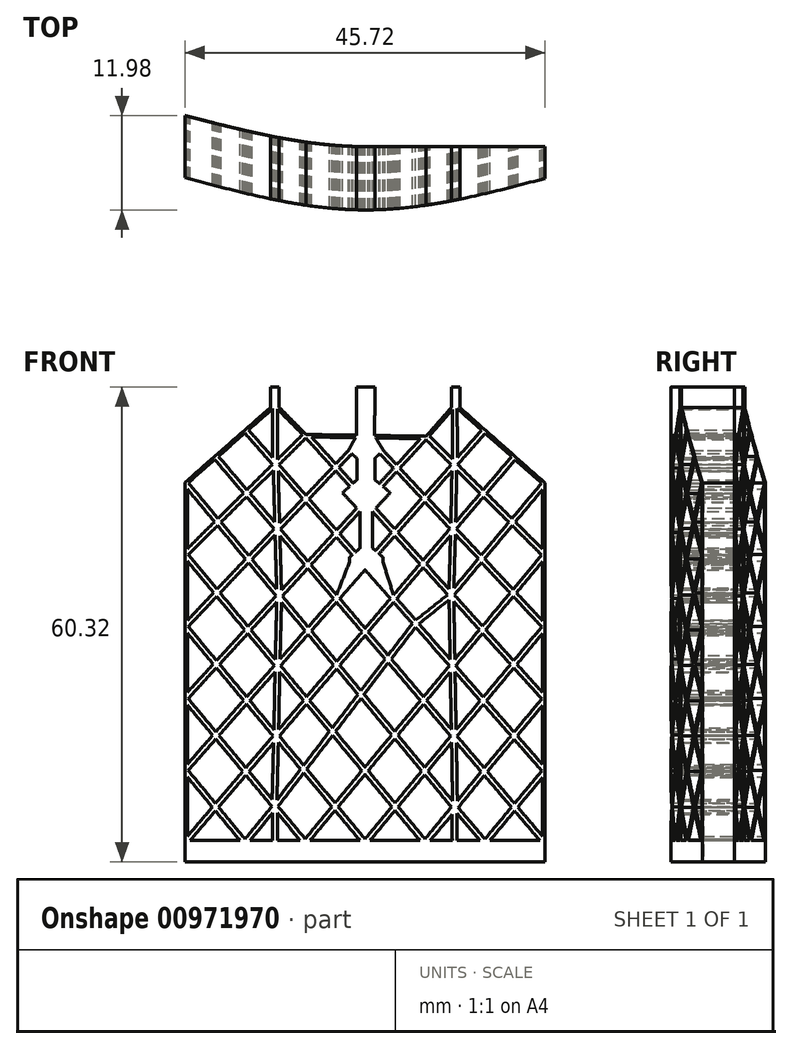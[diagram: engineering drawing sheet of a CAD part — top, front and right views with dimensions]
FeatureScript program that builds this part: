
annotation { "Feature Type Name" : "Feature", "Feature Type Description" : "" }
export const myFeature = defineFeature(function(context is Context, id is Id, definition is map)
    precondition{}
    {
        {
            var Q0;
            Q0=qCreatedBy(makeId("Top.planeOp"),FACE);
            var sketch = newSketch(context, id + "F0", { "sketchPlane" : qUnion([Q0])});
            skLineSegment(sketch, "E0", {"start": v(0, -22.65) * mm, "end": v(38.1, -22.65) * mm});
            skLineSegment(sketch, "E1", {"start": v(38.1, -22.65) * mm, "end": v(-38.1, -22.65) * mm});
            skLineSegment(sketch, "E2", {"start": v(38.1, -22.65) * mm, "end": v(38.1, -16.26) * mm});
            skLineSegment(sketch, "E3", {"start": v(38.1, -16.26) * mm, "end": v(38.1, -29.4) * mm});
            skLineSegment(sketch, "E4", {"start": v(-38.1, -22.65) * mm, "end": v(-38.1, -29.22) * mm});
            skLineSegment(sketch, "E5", {"start": v(-38.1, -29.22) * mm, "end": v(-38.1, -16.09) * mm});
            skPoint(sketch, "E6", {"position": v(-38.1, -22.65) * mm});
            skPoint(sketch, "E7", {"position": v(38.1, -22.82) * mm});
            skFitSpline(sketch, "E8", {"points": [v(-38.1, -16.09) * mm, v(0, -22.65) * mm, v(38.1, -16.26) * mm], "startDerivative": vector(76.18, -19.61) * mm, "endDerivative": vector(76.22, 19.27) * mm});
            skLineSegment(sketch, "E9", {"start": v(0, -22.65) * mm, "end": v(0, -36.06) * mm});
            skFitSpline(sketch, "E10", {"points": [v(-38.1, -29.22) * mm, v(0, -36.06) * mm, v(38.1, -29.4) * mm], "startDerivative": vector(76.18, -20.42) * mm, "endDerivative": vector(76.22, 20.08) * mm});
            skSolve(sketch);
        }
        {
            var Q0;
            Q0=qCreatedBy(makeId("Front.planeOp"),FACE);
            var sketch = newSketch(context, id + "F1", { "sketchPlane" : qUnion([Q0])});
            skLineSegment(sketch, "E11", {"start": v(38.1, -46.22) * mm, "end": v(25.4, -46.22) * mm, "construction": true});
            skLineSegment(sketch, "E12", {"start": v(-38.1, -46.22) * mm, "end": v(-38.1, -30.9) * mm, "construction": true});
            skLineSegment(sketch, "E13", {"start": v(38.1, 29.98) * mm, "end": v(38.1, 14.74) * mm, "construction": true});
            skLineSegment(sketch, "E14", {"start": v(-38.1, 30.06) * mm, "end": v(-31.74, 35.65) * mm, "construction": true});
            skLineSegment(sketch, "E15", {"start": v(38.1, 29.98) * mm, "end": v(31.76, 35.6) * mm, "construction": true});
            skLineSegment(sketch, "E16", {"start": v(-19.02, 46.83) * mm, "end": v(-12.48, 40.22) * mm, "construction": true});
            skLineSegment(sketch, "E17", {"start": v(19.08, 46.82) * mm, "end": v(12.92, 39.85) * mm, "construction": true});
            skLineSegment(sketch, "E18", {"start": v(-12.48, 40.22) * mm, "end": v(0.22, 40.04) * mm, "construction": true});
            skLineSegment(sketch, "E19", {"start": v(-25.38, 41.24) * mm, "end": v(-19.02, 46.83) * mm, "construction": true});
            skLineSegment(sketch, "E20", {"start": v(-31.74, 35.65) * mm, "end": v(-25.38, 41.24) * mm, "construction": true});
            skLineSegment(sketch, "E21", {"start": v(25.42, 41.2) * mm, "end": v(19.08, 46.82) * mm, "construction": true});
            skLineSegment(sketch, "E22", {"start": v(31.76, 35.6) * mm, "end": v(25.42, 41.2) * mm, "construction": true});
            skLineSegment(sketch, "E23", {"start": v(38.1, 14.74) * mm, "end": v(38.1, -0.5) * mm, "construction": true});
            skLineSegment(sketch, "E24", {"start": v(38.1, -0.5) * mm, "end": v(38.1, -15.74) * mm, "construction": true});
            skLineSegment(sketch, "E25", {"start": v(38.1, -15.74) * mm, "end": v(38.1, -30.98) * mm, "construction": true});
            skLineSegment(sketch, "E26", {"start": v(38.1, -30.98) * mm, "end": v(38.1, -46.22) * mm, "construction": true});
            skLineSegment(sketch, "E27", {"start": v(-38.1, 14.82) * mm, "end": v(-38.1, 30.06) * mm, "construction": true});
            skLineSegment(sketch, "E28", {"start": v(-38.1, -0.42) * mm, "end": v(-38.1, 14.82) * mm, "construction": true});
            skLineSegment(sketch, "E29", {"start": v(-38.1, -15.66) * mm, "end": v(-38.1, -0.42) * mm, "construction": true});
            skLineSegment(sketch, "E30", {"start": v(-38.1, -30.9) * mm, "end": v(-38.1, -15.66) * mm, "construction": true});
            skLineSegment(sketch, "E31", {"start": v(-25.4, -46.22) * mm, "end": v(-38.1, -46.22) * mm, "construction": true});
            skLineSegment(sketch, "E32", {"start": v(-12.64, -46.22) * mm, "end": v(-19.02, -46.22) * mm, "construction": true});
            skLineSegment(sketch, "E33", {"start": v(-50.8, 0) * mm, "end": v(-50.8, 0) * mm});
            skLineSegment(sketch, "E34", {"start": v(12.7, -46.22) * mm, "end": v(0, -46.22) * mm, "construction": true});
            skLineSegment(sketch, "E35", {"start": v(25.4, -46.22) * mm, "end": v(18.98, -46.22) * mm, "construction": true});
            skLineSegment(sketch, "E36", {"start": v(0, -46.22) * mm, "end": v(-12.7, -46.22) * mm, "construction": true});
            skLineSegment(sketch, "E37", {"start": v(12.92, 39.85) * mm, "end": v(18.94, 33.85) * mm, "construction": true});
            skPoint(sketch, "E38", {"position": v(0.22, 40.04) * mm});
            skLineSegment(sketch, "E39", {"start": v(-12.48, 40.22) * mm, "end": v(-6.2, 33.27) * mm, "construction": true});
            skLineSegment(sketch, "E40", {"start": v(0.22, 40.04) * mm, "end": v(6.7, 33.1) * mm, "construction": true});
            skLineSegment(sketch, "E41", {"start": v(-25.38, 41.24) * mm, "end": v(-18.99, 33.96) * mm, "construction": true});
            skLineSegment(sketch, "E42", {"start": v(-31.74, 35.65) * mm, "end": v(-25.03, 27.78) * mm, "construction": true});
            skLineSegment(sketch, "E43", {"start": v(-38.1, 30.06) * mm, "end": v(-31.16, 21.7) * mm, "construction": true});
            skLineSegment(sketch, "E44", {"start": v(-38.1, -0.42) * mm, "end": v(-31.45, -8.42) * mm, "construction": true});
            skLineSegment(sketch, "E45", {"start": v(-38.1, -15.66) * mm, "end": v(-31.58, -23.49) * mm, "construction": true});
            skLineSegment(sketch, "E46", {"start": v(-38.1, -30.9) * mm, "end": v(-31.66, -38.67) * mm, "construction": true});
            skLineSegment(sketch, "E47", {"start": v(-12.48, 40.22) * mm, "end": v(-18.9, 33.86) * mm, "construction": true});
            skLineSegment(sketch, "E48", {"start": v(0.22, 40.04) * mm, "end": v(-6.2, 33.27) * mm, "construction": true});
            skLineSegment(sketch, "E49", {"start": v(12.92, 39.85) * mm, "end": v(6.7, 33.1) * mm, "construction": true});
            skLineSegment(sketch, "E50", {"start": v(25.42, 41.2) * mm, "end": v(19.08, 34) * mm, "construction": true});
            skLineSegment(sketch, "E51", {"start": v(31.76, 35.6) * mm, "end": v(25.06, 27.75) * mm, "construction": true});
            skLineSegment(sketch, "E52", {"start": v(38.1, 29.98) * mm, "end": v(31.15, 21.68) * mm, "construction": true});
            skLineSegment(sketch, "E53", {"start": v(38.1, 14.74) * mm, "end": v(31.38, 6.68) * mm, "construction": true});
            skLineSegment(sketch, "E54", {"start": v(38.1, -0.5) * mm, "end": v(31.49, -8.43) * mm, "construction": true});
            skLineSegment(sketch, "E55", {"start": v(38.1, -30.98) * mm, "end": v(31.68, -38.69) * mm, "construction": true});
            skLineSegment(sketch, "E56", {"start": v(-38.1, 14.82) * mm, "end": v(-31.35, 6.7) * mm, "construction": true});
            skLineSegment(sketch, "E57", {"start": v(38.1, -15.74) * mm, "end": v(31.58, -23.56) * mm, "construction": true});
            skLineSegment(sketch, "E58", {"start": v(0.22, 40.04) * mm, "end": v(12.92, 39.85) * mm, "construction": true});
            skLineSegment(sketch, "E59", {"start": v(19.08, 34) * mm, "end": v(18.94, 33.85) * mm, "construction": true});
            skLineSegment(sketch, "E60", {"start": v(18.94, 33.85) * mm, "end": v(19.08, 33.71) * mm, "construction": true});
            skLineSegment(sketch, "E61", {"start": v(19.08, 33.71) * mm, "end": v(25.06, 27.75) * mm, "construction": true});
            skLineSegment(sketch, "E62", {"start": v(18.67, 20.27) * mm, "end": v(12.3, 12.81) * mm, "construction": true});
            skLineSegment(sketch, "E63", {"start": v(18.54, -8.73) * mm, "end": v(12.4, -16.1) * mm, "construction": true});
            skLineSegment(sketch, "E64", {"start": v(18.83, -23.63) * mm, "end": v(12.64, -31.04) * mm, "construction": true});
            skLineSegment(sketch, "E65", {"start": v(18.98, -46.22) * mm, "end": v(12.7, -46.22) * mm, "construction": true});
            skLineSegment(sketch, "E66", {"start": v(18.94, 33.85) * mm, "end": v(12.66, 26.71) * mm, "construction": true});
            skLineSegment(sketch, "E67", {"start": v(25.06, 27.75) * mm, "end": v(18.67, 20.27) * mm, "construction": true});
            skLineSegment(sketch, "E68", {"start": v(25.06, 27.75) * mm, "end": v(31.15, 21.68) * mm, "construction": true});
            skLineSegment(sketch, "E69", {"start": v(31.15, 21.68) * mm, "end": v(24.67, 13.94) * mm, "construction": true});
            skLineSegment(sketch, "E70", {"start": v(31.15, 21.68) * mm, "end": v(38.1, 14.74) * mm, "construction": true});
            skLineSegment(sketch, "E71.0", {"start": v(24.7, 41.16) * mm, "end": v(19.5, 45.76) * mm});
            skLineSegment(sketch, "E71.1", {"start": v(24.7, 41.16) * mm, "end": v(19.59, 35.35) * mm});
            skLineSegment(sketch, "E71.2", {"start": v(19.5, 45.76) * mm, "end": v(19.59, 35.35) * mm});
            skLineSegment(sketch, "E72.0", {"start": v(18.56, 45.52) * mm, "end": v(18.56, 35.03) * mm});
            skLineSegment(sketch, "E72.1", {"start": v(18.56, 45.52) * mm, "end": v(13.63, 39.95) * mm});
            skLineSegment(sketch, "E72.2", {"start": v(13.63, 39.95) * mm, "end": v(18.56, 35.03) * mm});
            skLineSegment(sketch, "E73.0", {"start": v(31.05, 35.54) * mm, "end": v(25.46, 40.49) * mm});
            skLineSegment(sketch, "E73.1", {"start": v(31.05, 35.54) * mm, "end": v(25.03, 28.5) * mm});
            skLineSegment(sketch, "E73.2", {"start": v(19.64, 33.87) * mm, "end": v(25.03, 28.5) * mm});
            skLineSegment(sketch, "E73.3", {"start": v(25.46, 40.49) * mm, "end": v(19.64, 33.87) * mm});
            skLineSegment(sketch, "E74.0", {"start": v(37.4, 29.93) * mm, "end": v(31.8, 34.87) * mm});
            skLineSegment(sketch, "E74.1", {"start": v(37.4, 29.93) * mm, "end": v(31.11, 22.43) * mm});
            skLineSegment(sketch, "E74.2", {"start": v(25.75, 27.77) * mm, "end": v(31.11, 22.43) * mm});
            skLineSegment(sketch, "E74.3", {"start": v(31.8, 34.87) * mm, "end": v(25.75, 27.77) * mm});
            skLineSegment(sketch, "E75.0", {"start": v(37.6, 28.58) * mm, "end": v(37.6, 15.97) * mm});
            skLineSegment(sketch, "E75.1", {"start": v(37.6, 28.58) * mm, "end": v(31.83, 21.7) * mm});
            skLineSegment(sketch, "E75.2", {"start": v(31.83, 21.7) * mm, "end": v(37.6, 15.97) * mm});
            skLineSegment(sketch, "E76", {"start": v(-18.99, 33.96) * mm, "end": v(-18.9, 33.86) * mm, "construction": true});
            skLineSegment(sketch, "E77", {"start": v(-18.9, 33.86) * mm, "end": v(-19.02, 33.73) * mm, "construction": true});
            skLineSegment(sketch, "E78", {"start": v(-18.9, 33.86) * mm, "end": v(-12.51, 26.6) * mm, "construction": true});
            skLineSegment(sketch, "E79", {"start": v(-19.02, 33.73) * mm, "end": v(-25.03, 27.78) * mm, "construction": true});
            skLineSegment(sketch, "E80", {"start": v(-18.57, 20.2) * mm, "end": v(-12.1, 12.63) * mm, "construction": true});
            skLineSegment(sketch, "E81", {"start": v(-18.57, 20.2) * mm, "end": v(-24.61, 13.82) * mm, "construction": true});
            skLineSegment(sketch, "E82", {"start": v(-18.15, 6.04) * mm, "end": v(-12.03, -1.33) * mm, "construction": true});
            skLineSegment(sketch, "E83", {"start": v(-18.15, 6.04) * mm, "end": v(-24.8, -1.19) * mm, "construction": true});
            skLineSegment(sketch, "E84", {"start": v(-18.8, -23.62) * mm, "end": v(-12.98, -30.62) * mm, "construction": true});
            skLineSegment(sketch, "E85", {"start": v(-18.8, -23.62) * mm, "end": v(-25.23, -31.14) * mm, "construction": true});
            skLineSegment(sketch, "E86", {"start": v(-19.19, -38.36) * mm, "end": v(-12.64, -46.22) * mm, "construction": true});
            skLineSegment(sketch, "E87", {"start": v(-19.05, -38.52) * mm, "end": v(-25.4, -46.22) * mm, "construction": true});
            skLineSegment(sketch, "E88", {"start": v(-19.02, -46.22) * mm, "end": v(-25.4, -46.22) * mm, "construction": true});
            skLineSegment(sketch, "E89", {"start": v(-25.03, 27.78) * mm, "end": v(-18.57, 20.2) * mm, "construction": true});
            skLineSegment(sketch, "E90", {"start": v(-25.03, 27.78) * mm, "end": v(-31.16, 21.7) * mm, "construction": true});
            skLineSegment(sketch, "E91", {"start": v(-31.16, 21.7) * mm, "end": v(-24.61, 13.82) * mm, "construction": true});
            skLineSegment(sketch, "E92", {"start": v(-31.16, 21.7) * mm, "end": v(-38.1, 14.82) * mm, "construction": true});
            skLineSegment(sketch, "E93.0", {"start": v(-37.4, 30) * mm, "end": v(-31.8, 34.93) * mm});
            skLineSegment(sketch, "E93.1", {"start": v(-37.4, 30) * mm, "end": v(-31.12, 22.45) * mm});
            skLineSegment(sketch, "E93.2", {"start": v(-25.72, 27.8) * mm, "end": v(-31.12, 22.45) * mm});
            skLineSegment(sketch, "E93.3", {"start": v(-31.8, 34.93) * mm, "end": v(-25.72, 27.8) * mm});
            skLineSegment(sketch, "E94.0", {"start": v(-37.6, 28.65) * mm, "end": v(-31.85, 21.73) * mm});
            skLineSegment(sketch, "E94.1", {"start": v(-37.6, 16.04) * mm, "end": v(-37.6, 28.65) * mm});
            skLineSegment(sketch, "E94.2", {"start": v(-31.85, 21.73) * mm, "end": v(-37.6, 16.04) * mm});
            skLineSegment(sketch, "E95", {"start": v(-6.2, 33.27) * mm, "end": v(0.28, 26.1) * mm, "construction": true});
            skLineSegment(sketch, "E96", {"start": v(-6.2, 33.27) * mm, "end": v(-12.51, 26.6) * mm, "construction": true});
            skLineSegment(sketch, "E97", {"start": v(6.7, 33.1) * mm, "end": v(12.66, 26.71) * mm, "construction": true});
            skLineSegment(sketch, "E98", {"start": v(6.7, 33.1) * mm, "end": v(0.28, 26.1) * mm, "construction": true});
            skLineSegment(sketch, "E99.0", {"start": v(-11.32, 39.7) * mm, "end": v(-6.18, 34.02) * mm});
            skLineSegment(sketch, "E99.1", {"start": v(-11.32, 39.7) * mm, "end": v(-0.95, 39.55) * mm});
            skLineSegment(sketch, "E99.2", {"start": v(-0.95, 39.55) * mm, "end": v(-6.18, 34.02) * mm});
            skLineSegment(sketch, "E100.0", {"start": v(1.4, 39.51) * mm, "end": v(11.78, 39.36) * mm});
            skLineSegment(sketch, "E100.1", {"start": v(1.4, 39.51) * mm, "end": v(6.7, 33.84) * mm});
            skLineSegment(sketch, "E100.2", {"start": v(11.78, 39.36) * mm, "end": v(6.7, 33.84) * mm});
            skLineSegment(sketch, "E101", {"start": v(0.28, 26.1) * mm, "end": v(-6.04, 19.23) * mm, "construction": true});
            skLineSegment(sketch, "E102", {"start": v(0.28, 26.1) * mm, "end": v(6.28, 19.47) * mm, "construction": true});
            skLineSegment(sketch, "E103", {"start": v(-12.51, 26.6) * mm, "end": v(-18.57, 20.2) * mm, "construction": true});
            skLineSegment(sketch, "E104", {"start": v(-6.04, 19.23) * mm, "end": v(-12.1, 12.63) * mm, "construction": true});
            skLineSegment(sketch, "E105", {"start": v(-6.04, 19.23) * mm, "end": v(0.01, 12.35) * mm, "construction": true});
            skLineSegment(sketch, "E106", {"start": v(-12.51, 26.6) * mm, "end": v(-6.04, 19.23) * mm, "construction": true});
            skLineSegment(sketch, "E107", {"start": v(12.66, 26.71) * mm, "end": v(18.67, 20.27) * mm, "construction": true});
            skLineSegment(sketch, "E108", {"start": v(12.66, 26.71) * mm, "end": v(6.28, 19.47) * mm, "construction": true});
            skLineSegment(sketch, "E109", {"start": v(6.28, 19.47) * mm, "end": v(0.01, 12.35) * mm, "construction": true});
            skLineSegment(sketch, "E110", {"start": v(6.28, 19.47) * mm, "end": v(12.3, 12.81) * mm, "construction": true});
            skLineSegment(sketch, "E111.0", {"start": v(12.93, 39.12) * mm, "end": v(18.24, 33.82) * mm});
            skLineSegment(sketch, "E111.1", {"start": v(12.93, 39.12) * mm, "end": v(7.4, 33.1) * mm});
            skLineSegment(sketch, "E111.2", {"start": v(7.4, 33.1) * mm, "end": v(12.65, 27.47) * mm});
            skLineSegment(sketch, "E111.3", {"start": v(18.24, 33.82) * mm, "end": v(12.65, 27.47) * mm});
            skLineSegment(sketch, "E112.0", {"start": v(6.7, 32.34) * mm, "end": v(11.97, 26.7) * mm});
            skLineSegment(sketch, "E112.1", {"start": v(6.7, 32.34) * mm, "end": v(0.97, 26.1) * mm});
            skLineSegment(sketch, "E112.2", {"start": v(0.97, 26.1) * mm, "end": v(6.28, 20.24) * mm});
            skLineSegment(sketch, "E112.3", {"start": v(11.97, 26.7) * mm, "end": v(6.28, 20.24) * mm});
            skLineSegment(sketch, "E113.0", {"start": v(0.22, 39.3) * mm, "end": v(6, 33.09) * mm});
            skLineSegment(sketch, "E113.1", {"start": v(0.22, 39.3) * mm, "end": v(-5.5, 33.26) * mm});
            skLineSegment(sketch, "E113.2", {"start": v(-5.5, 33.26) * mm, "end": v(0.29, 26.86) * mm});
            skLineSegment(sketch, "E113.3", {"start": v(6, 33.09) * mm, "end": v(0.29, 26.86) * mm});
            skLineSegment(sketch, "E114.0", {"start": v(-6.2, 32.52) * mm, "end": v(-0.4, 26.1) * mm});
            skLineSegment(sketch, "E114.1", {"start": v(-6.2, 32.52) * mm, "end": v(-11.82, 26.58) * mm});
            skLineSegment(sketch, "E114.2", {"start": v(-11.82, 26.58) * mm, "end": v(-6.03, 19.99) * mm});
            skLineSegment(sketch, "E114.3", {"start": v(-0.4, 26.1) * mm, "end": v(-6.03, 19.99) * mm});
            skLineSegment(sketch, "E115.0", {"start": v(-6.88, 33.28) * mm, "end": v(-12.5, 27.35) * mm});
            skLineSegment(sketch, "E115.1", {"start": v(-12.5, 39.49) * mm, "end": v(-6.88, 33.28) * mm});
            skLineSegment(sketch, "E115.2", {"start": v(-12.5, 39.49) * mm, "end": v(-18.2, 33.84) * mm});
            skLineSegment(sketch, "E115.3", {"start": v(-18.2, 33.84) * mm, "end": v(-12.5, 27.35) * mm});
            skLineSegment(sketch, "E116.0", {"start": v(-18.51, 45.6) * mm, "end": v(-13.2, 40.22) * mm});
            skLineSegment(sketch, "E116.1", {"start": v(-18.51, 45.6) * mm, "end": v(-18.51, 34.95) * mm});
            skLineSegment(sketch, "E116.2", {"start": v(-13.2, 40.22) * mm, "end": v(-18.51, 34.95) * mm});
            skLineSegment(sketch, "E117.0", {"start": v(-19.53, 45.7) * mm, "end": v(-19.53, 35.36) * mm});
            skLineSegment(sketch, "E117.1", {"start": v(-24.66, 41.2) * mm, "end": v(-19.53, 45.7) * mm});
            skLineSegment(sketch, "E117.2", {"start": v(-24.66, 41.2) * mm, "end": v(-19.53, 35.36) * mm});
            skLineSegment(sketch, "E118.0", {"start": v(-25.43, 40.52) * mm, "end": v(-19.6, 33.88) * mm});
            skLineSegment(sketch, "E118.1", {"start": v(-31.03, 35.6) * mm, "end": v(-25.43, 40.52) * mm});
            skLineSegment(sketch, "E118.2", {"start": v(-31.03, 35.6) * mm, "end": v(-25, 28.53) * mm});
            skLineSegment(sketch, "E118.3", {"start": v(-19.6, 33.88) * mm, "end": v(-25, 28.53) * mm});
            skLineSegment(sketch, "E119", {"start": v(31.38, 6.68) * mm, "end": v(24.89, -1.11) * mm, "construction": true});
            skLineSegment(sketch, "E120", {"start": v(31.38, 6.68) * mm, "end": v(38.1, -0.5) * mm, "construction": true});
            skLineSegment(sketch, "E121", {"start": v(31.49, -8.43) * mm, "end": v(25.06, -16.14) * mm, "construction": true});
            skLineSegment(sketch, "E122", {"start": v(31.49, -8.43) * mm, "end": v(38.1, -15.74) * mm, "construction": true});
            skLineSegment(sketch, "E123", {"start": v(31.58, -23.56) * mm, "end": v(25.25, -31.16) * mm, "construction": true});
            skLineSegment(sketch, "E124", {"start": v(31.58, -23.56) * mm, "end": v(38.1, -30.98) * mm, "construction": true});
            skLineSegment(sketch, "E125", {"start": v(31.68, -38.69) * mm, "end": v(25.4, -46.22) * mm, "construction": true});
            skLineSegment(sketch, "E126", {"start": v(31.68, -38.69) * mm, "end": v(38.1, -46.22) * mm, "construction": true});
            skLineSegment(sketch, "E127.0", {"start": v(37.6, 13.35) * mm, "end": v(32.05, 6.7) * mm});
            skLineSegment(sketch, "E127.1", {"start": v(37.6, 13.35) * mm, "end": v(37.6, 0.78) * mm});
            skLineSegment(sketch, "E127.2", {"start": v(32.05, 6.7) * mm, "end": v(37.6, 0.78) * mm});
            skLineSegment(sketch, "E128.0", {"start": v(37.6, -1.9) * mm, "end": v(32.16, -8.42) * mm});
            skLineSegment(sketch, "E128.1", {"start": v(37.6, -1.9) * mm, "end": v(37.6, -14.42) * mm});
            skLineSegment(sketch, "E128.2", {"start": v(32.16, -8.42) * mm, "end": v(37.6, -14.42) * mm});
            skLineSegment(sketch, "E129.0", {"start": v(37.6, -17.14) * mm, "end": v(32.25, -23.55) * mm});
            skLineSegment(sketch, "E129.1", {"start": v(37.6, -17.14) * mm, "end": v(37.6, -29.63) * mm});
            skLineSegment(sketch, "E129.2", {"start": v(32.25, -23.55) * mm, "end": v(37.6, -29.63) * mm});
            skLineSegment(sketch, "E130.0", {"start": v(37.6, -32.38) * mm, "end": v(32.34, -38.68) * mm});
            skLineSegment(sketch, "E130.1", {"start": v(37.6, -32.38) * mm, "end": v(37.6, -44.84) * mm});
            skLineSegment(sketch, "E130.2", {"start": v(32.34, -38.68) * mm, "end": v(37.6, -44.84) * mm});
            skLineSegment(sketch, "E131", {"start": v(-31.35, 6.7) * mm, "end": v(-24.79, -1.18) * mm, "construction": true});
            skLineSegment(sketch, "E132", {"start": v(-31.35, 6.7) * mm, "end": v(-38.1, -0.42) * mm, "construction": true});
            skLineSegment(sketch, "E133", {"start": v(-31.45, -8.42) * mm, "end": v(-25.05, -16.11) * mm, "construction": true});
            skLineSegment(sketch, "E134", {"start": v(-31.45, -8.42) * mm, "end": v(-38.1, -15.66) * mm, "construction": true});
            skLineSegment(sketch, "E135", {"start": v(-31.58, -23.49) * mm, "end": v(-25.21, -31.13) * mm, "construction": true});
            skLineSegment(sketch, "E136", {"start": v(-31.58, -23.49) * mm, "end": v(-38.1, -30.9) * mm, "construction": true});
            skLineSegment(sketch, "E137", {"start": v(-31.66, -38.67) * mm, "end": v(-38.1, -46.22) * mm, "construction": true});
            skLineSegment(sketch, "E138", {"start": v(-31.66, -38.67) * mm, "end": v(-25.4, -46.22) * mm, "construction": true});
            skLineSegment(sketch, "E139.0", {"start": v(-37.6, 13.41) * mm, "end": v(-32.03, 6.73) * mm});
            skLineSegment(sketch, "E139.1", {"start": v(-37.6, 0.85) * mm, "end": v(-37.6, 13.41) * mm});
            skLineSegment(sketch, "E139.2", {"start": v(-32.03, 6.73) * mm, "end": v(-37.6, 0.85) * mm});
            skLineSegment(sketch, "E140.0", {"start": v(-37.6, -1.83) * mm, "end": v(-32.12, -8.4) * mm});
            skLineSegment(sketch, "E140.1", {"start": v(-37.6, -14.36) * mm, "end": v(-37.6, -1.83) * mm});
            skLineSegment(sketch, "E140.2", {"start": v(-32.12, -8.4) * mm, "end": v(-37.6, -14.36) * mm});
            skLineSegment(sketch, "E141.0", {"start": v(-37.6, -17.04) * mm, "end": v(-32.24, -23.48) * mm});
            skLineSegment(sketch, "E141.1", {"start": v(-37.6, -29.58) * mm, "end": v(-37.6, -17.04) * mm});
            skLineSegment(sketch, "E141.2", {"start": v(-32.24, -23.48) * mm, "end": v(-37.6, -29.58) * mm});
            skLineSegment(sketch, "E142.0", {"start": v(-37.6, -44.85) * mm, "end": v(-37.6, -32.3) * mm});
            skLineSegment(sketch, "E142.1", {"start": v(-32.31, -38.67) * mm, "end": v(-37.6, -44.85) * mm});
            skLineSegment(sketch, "E142.2", {"start": v(-37.6, -32.3) * mm, "end": v(-32.31, -38.67) * mm});
            skLineSegment(sketch, "E143.0", {"start": v(-31.66, -39.46) * mm, "end": v(-37, -45.7) * mm});
            skLineSegment(sketch, "E143.1", {"start": v(-31.66, -39.46) * mm, "end": v(-26.48, -45.7) * mm});
            skLineSegment(sketch, "E143.2", {"start": v(-26.48, -45.7) * mm, "end": v(-37, -45.7) * mm});
            skLineSegment(sketch, "E144", {"start": v(-6.34, -38.6) * mm, "end": v(0, -46.22) * mm, "construction": true});
            skLineSegment(sketch, "E145", {"start": v(-6.34, -38.6) * mm, "end": v(-12.7, -46.22) * mm, "construction": true});
            skLineSegment(sketch, "E146.0", {"start": v(-6.35, -39.38) * mm, "end": v(-11.62, -45.7) * mm});
            skLineSegment(sketch, "E146.1", {"start": v(-6.35, -39.38) * mm, "end": v(-1.08, -45.7) * mm});
            skLineSegment(sketch, "E146.2", {"start": v(-1.08, -45.7) * mm, "end": v(-11.62, -45.7) * mm});
            skLineSegment(sketch, "E147.0", {"start": v(37, -45.7) * mm, "end": v(26.48, -45.7) * mm});
            skLineSegment(sketch, "E147.1", {"start": v(31.68, -39.47) * mm, "end": v(37, -45.7) * mm});
            skLineSegment(sketch, "E147.2", {"start": v(31.68, -39.47) * mm, "end": v(26.48, -45.7) * mm});
            skLineSegment(sketch, "E148", {"start": v(-24.61, 13.82) * mm, "end": v(-18.15, 6.04) * mm, "construction": true});
            skLineSegment(sketch, "E149", {"start": v(-24.61, 13.82) * mm, "end": v(-31.35, 6.7) * mm, "construction": true});
            skLineSegment(sketch, "E150", {"start": v(-24.8, -1.19) * mm, "end": v(-31.45, -8.42) * mm, "construction": true});
            skLineSegment(sketch, "E151", {"start": v(-25.05, -16.11) * mm, "end": v(-18.8, -23.62) * mm, "construction": true});
            skLineSegment(sketch, "E152", {"start": v(-25.07, -16.09) * mm, "end": v(-31.58, -23.49) * mm, "construction": true});
            skLineSegment(sketch, "E153", {"start": v(-25.23, -31.14) * mm, "end": v(-31.66, -38.67) * mm, "construction": true});
            skLineSegment(sketch, "E154", {"start": v(-25.21, -31.13) * mm, "end": v(-19.19, -38.36) * mm, "construction": true});
            skLineSegment(sketch, "E155.0", {"start": v(-31.2, 20.95) * mm, "end": v(-25.3, 13.84) * mm});
            skLineSegment(sketch, "E155.1", {"start": v(-31.2, 20.95) * mm, "end": v(-37.41, 14.79) * mm});
            skLineSegment(sketch, "E155.2", {"start": v(-37.41, 14.79) * mm, "end": v(-31.32, 7.47) * mm});
            skLineSegment(sketch, "E155.3", {"start": v(-25.3, 13.84) * mm, "end": v(-31.32, 7.47) * mm});
            skLineSegment(sketch, "E156", {"start": v(-24.79, -1.18) * mm, "end": v(-18.53, -8.7) * mm, "construction": true});
            skLineSegment(sketch, "E157.0", {"start": v(-31.37, 5.94) * mm, "end": v(-25.46, -1.16) * mm});
            skLineSegment(sketch, "E157.1", {"start": v(-31.37, 5.94) * mm, "end": v(-37.42, -0.44) * mm});
            skLineSegment(sketch, "E157.2", {"start": v(-37.42, -0.44) * mm, "end": v(-31.43, -7.65) * mm});
            skLineSegment(sketch, "E157.3", {"start": v(-25.46, -1.16) * mm, "end": v(-31.43, -7.65) * mm});
            skLineSegment(sketch, "E158.0", {"start": v(-31.46, -9.18) * mm, "end": v(-25.72, -16.08) * mm});
            skLineSegment(sketch, "E158.1", {"start": v(-31.46, -9.18) * mm, "end": v(-37.44, -15.68) * mm});
            skLineSegment(sketch, "E158.2", {"start": v(-37.44, -15.68) * mm, "end": v(-31.57, -22.72) * mm});
            skLineSegment(sketch, "E158.3", {"start": v(-25.72, -16.08) * mm, "end": v(-31.57, -22.72) * mm});
            skLineSegment(sketch, "E159.0", {"start": v(-31.59, -24.27) * mm, "end": v(-25.88, -31.12) * mm});
            skLineSegment(sketch, "E159.1", {"start": v(-31.59, -24.27) * mm, "end": v(-37.43, -30.91) * mm});
            skLineSegment(sketch, "E159.2", {"start": v(-37.43, -30.91) * mm, "end": v(-31.65, -37.88) * mm});
            skLineSegment(sketch, "E159.3", {"start": v(-25.88, -31.12) * mm, "end": v(-31.65, -37.88) * mm});
            skLineSegment(sketch, "E160", {"start": v(24.63, 13.9) * mm, "end": v(31.38, 6.68) * mm, "construction": true});
            skLineSegment(sketch, "E161", {"start": v(24.89, -1.11) * mm, "end": v(18.54, -8.73) * mm, "construction": true});
            skLineSegment(sketch, "E162", {"start": v(24.88, -1.13) * mm, "end": v(31.49, -8.43) * mm, "construction": true});
            skLineSegment(sketch, "E163", {"start": v(25.06, -16.14) * mm, "end": v(18.83, -23.63) * mm, "construction": true});
            skLineSegment(sketch, "E164", {"start": v(25.06, -16.14) * mm, "end": v(31.58, -23.56) * mm, "construction": true});
            skLineSegment(sketch, "E165", {"start": v(25.25, -31.16) * mm, "end": v(31.68, -38.69) * mm, "construction": true});
            skLineSegment(sketch, "E166.0", {"start": v(31.18, 20.93) * mm, "end": v(25.3, 13.91) * mm});
            skLineSegment(sketch, "E166.1", {"start": v(31.18, 20.93) * mm, "end": v(37.41, 14.71) * mm});
            skLineSegment(sketch, "E166.2", {"start": v(37.41, 14.71) * mm, "end": v(31.36, 7.45) * mm});
            skLineSegment(sketch, "E166.3", {"start": v(25.3, 13.91) * mm, "end": v(31.36, 7.45) * mm});
            skLineSegment(sketch, "E167.0", {"start": v(31.4, 5.92) * mm, "end": v(25.55, -1.11) * mm});
            skLineSegment(sketch, "E167.1", {"start": v(31.4, 5.92) * mm, "end": v(37.42, -0.52) * mm});
            skLineSegment(sketch, "E167.2", {"start": v(37.42, -0.52) * mm, "end": v(31.47, -7.66) * mm});
            skLineSegment(sketch, "E167.3", {"start": v(25.55, -1.11) * mm, "end": v(31.47, -7.66) * mm});
            skLineSegment(sketch, "E168.0", {"start": v(31.5, -9.2) * mm, "end": v(25.73, -16.14) * mm});
            skLineSegment(sketch, "E168.1", {"start": v(31.5, -9.2) * mm, "end": v(37.43, -15.75) * mm});
            skLineSegment(sketch, "E168.2", {"start": v(37.43, -15.75) * mm, "end": v(31.57, -22.78) * mm});
            skLineSegment(sketch, "E168.3", {"start": v(25.73, -16.14) * mm, "end": v(31.57, -22.78) * mm});
            skLineSegment(sketch, "E169.0", {"start": v(31.6, -24.34) * mm, "end": v(25.92, -31.15) * mm});
            skLineSegment(sketch, "E169.1", {"start": v(31.6, -24.34) * mm, "end": v(37.43, -30.99) * mm});
            skLineSegment(sketch, "E169.2", {"start": v(37.43, -30.99) * mm, "end": v(31.67, -37.9) * mm});
            skLineSegment(sketch, "E169.3", {"start": v(25.92, -31.15) * mm, "end": v(31.67, -37.9) * mm});
            skLineSegment(sketch, "E170", {"start": v(0.01, 12.35) * mm, "end": v(6.05, 5.48) * mm, "construction": true});
            skLineSegment(sketch, "E171", {"start": v(0.01, 12.35) * mm, "end": v(-6.02, 5.5) * mm, "construction": true});
            skLineSegment(sketch, "E172.0", {"start": v(-5.35, 19.22) * mm, "end": v(0.01, 13.12) * mm});
            skLineSegment(sketch, "E172.1", {"start": v(0.28, 25.35) * mm, "end": v(-5.35, 19.22) * mm});
            skLineSegment(sketch, "E172.2", {"start": v(0.28, 25.35) * mm, "end": v(5.6, 19.47) * mm});
            skLineSegment(sketch, "E172.3", {"start": v(5.6, 19.47) * mm, "end": v(0.01, 13.12) * mm});
            skLineSegment(sketch, "E173", {"start": v(-12.1, 12.63) * mm, "end": v(-18.15, 6.04) * mm, "construction": true});
            skLineSegment(sketch, "E174", {"start": v(-6.02, 5.5) * mm, "end": v(-12.03, -1.33) * mm, "construction": true});
            skLineSegment(sketch, "E175", {"start": v(-12.1, 12.63) * mm, "end": v(-6.02, 5.5) * mm, "construction": true});
            skLineSegment(sketch, "E176", {"start": v(-6.02, 5.5) * mm, "end": v(0.02, -1.58) * mm, "construction": true});
            skLineSegment(sketch, "E177", {"start": v(12.3, 12.81) * mm, "end": v(18.3, 6.2) * mm, "construction": true});
            skLineSegment(sketch, "E178", {"start": v(6.05, 5.48) * mm, "end": v(0.02, -1.58) * mm, "construction": true});
            skLineSegment(sketch, "E179", {"start": v(6.05, 5.48) * mm, "end": v(11.99, -1.27) * mm, "construction": true});
            skLineSegment(sketch, "E180", {"start": v(12.3, 12.81) * mm, "end": v(6.05, 5.48) * mm, "construction": true});
            skLineSegment(sketch, "E181.0", {"start": v(-6.04, 18.47) * mm, "end": v(-11.42, 12.62) * mm});
            skLineSegment(sketch, "E181.1", {"start": v(-6.04, 18.47) * mm, "end": v(-0.66, 12.35) * mm});
            skLineSegment(sketch, "E181.2", {"start": v(-0.66, 12.35) * mm, "end": v(-6.01, 6.28) * mm});
            skLineSegment(sketch, "E181.3", {"start": v(-11.42, 12.62) * mm, "end": v(-6.01, 6.28) * mm});
            skLineSegment(sketch, "E182.0", {"start": v(6.29, 18.71) * mm, "end": v(0.69, 12.35) * mm});
            skLineSegment(sketch, "E182.1", {"start": v(6.29, 18.71) * mm, "end": v(11.63, 12.8) * mm});
            skLineSegment(sketch, "E182.2", {"start": v(11.63, 12.8) * mm, "end": v(6.04, 6.26) * mm});
            skLineSegment(sketch, "E182.3", {"start": v(0.69, 12.35) * mm, "end": v(6.04, 6.26) * mm});
            skLineSegment(sketch, "E183", {"start": v(0.02, -1.58) * mm, "end": v(-5.99, -8.6) * mm, "construction": true});
            skLineSegment(sketch, "E184", {"start": v(0.02, -1.58) * mm, "end": v(5.98, -8.57) * mm, "construction": true});
            skLineSegment(sketch, "E185.0", {"start": v(0.01, 11.58) * mm, "end": v(-5.35, 5.5) * mm});
            skLineSegment(sketch, "E185.1", {"start": v(0.01, 11.58) * mm, "end": v(5.38, 5.48) * mm});
            skLineSegment(sketch, "E185.2", {"start": v(5.38, 5.48) * mm, "end": v(0.02, -0.8) * mm});
            skLineSegment(sketch, "E185.3", {"start": v(-5.35, 5.5) * mm, "end": v(0.02, -0.8) * mm});
            skLineSegment(sketch, "E186", {"start": v(5.98, -8.57) * mm, "end": v(12.4, -16.1) * mm, "construction": true});
            skLineSegment(sketch, "E187", {"start": v(11.99, -1.27) * mm, "end": v(18.52, -8.7) * mm, "construction": true});
            skLineSegment(sketch, "E188", {"start": v(10.68, 0.2) * mm, "end": v(4.9, -7.31) * mm, "construction": true});
            skLineSegment(sketch, "E189", {"start": v(4.9, -7.31) * mm, "end": v(-0.84, -14.8) * mm, "construction": true});
            skLineSegment(sketch, "E190.0", {"start": v(6.05, 4.7) * mm, "end": v(0.69, -1.58) * mm});
            skLineSegment(sketch, "E190.1", {"start": v(6.05, 4.7) * mm, "end": v(10.03, 0.19) * mm});
            skLineSegment(sketch, "E190.2", {"start": v(10.03, 0.19) * mm, "end": v(4.89, -6.5) * mm});
            skLineSegment(sketch, "E190.3", {"start": v(0.69, -1.58) * mm, "end": v(4.89, -6.5) * mm});
            skLineSegment(sketch, "E191", {"start": v(-12.03, -1.33) * mm, "end": v(-18.53, -8.7) * mm, "construction": true});
            skLineSegment(sketch, "E192", {"start": v(-12.03, -1.33) * mm, "end": v(-5.99, -8.6) * mm, "construction": true});
            skLineSegment(sketch, "E193", {"start": v(-5.99, -8.6) * mm, "end": v(-0.84, -14.8) * mm, "construction": true});
            skLineSegment(sketch, "E194", {"start": v(-5.99, -8.6) * mm, "end": v(-12.4, -16.11) * mm, "construction": true});
            skLineSegment(sketch, "E195.0", {"start": v(-6.03, 4.72) * mm, "end": v(-11.37, -1.34) * mm});
            skLineSegment(sketch, "E195.1", {"start": v(-6.03, 4.72) * mm, "end": v(-0.65, -1.58) * mm});
            skLineSegment(sketch, "E195.2", {"start": v(-0.65, -1.58) * mm, "end": v(-5.98, -7.82) * mm});
            skLineSegment(sketch, "E195.3", {"start": v(-11.37, -1.34) * mm, "end": v(-5.98, -7.82) * mm});
            skLineSegment(sketch, "E196", {"start": v(-0.84, -14.8) * mm, "end": v(6.3, -23.41) * mm, "construction": true});
            skLineSegment(sketch, "E197", {"start": v(-0.84, -14.8) * mm, "end": v(-6.89, -22.68) * mm, "construction": true});
            skLineSegment(sketch, "E198", {"start": v(12.4, -16.1) * mm, "end": v(18.83, -23.63) * mm, "construction": true});
            skLineSegment(sketch, "E199", {"start": v(6.3, -23.41) * mm, "end": v(-0.02, -31) * mm, "construction": true});
            skLineSegment(sketch, "E200", {"start": v(6.3, -23.41) * mm, "end": v(12.64, -31.04) * mm, "construction": true});
            skLineSegment(sketch, "E201", {"start": v(-6.89, -22.68) * mm, "end": v(-12.97, -30.6) * mm, "construction": true});
            skLineSegment(sketch, "E202", {"start": v(-12.4, -16.11) * mm, "end": v(-18.8, -23.62) * mm, "construction": true});
            skLineSegment(sketch, "E203", {"start": v(-12.37, -16.1) * mm, "end": v(-6.89, -22.68) * mm, "construction": true});
            skLineSegment(sketch, "E204", {"start": v(-6.89, -22.68) * mm, "end": v(0, -30.97) * mm, "construction": true});
            skLineSegment(sketch, "E205.0", {"start": v(4.26, -7.33) * mm, "end": v(-0.86, -14) * mm});
            skLineSegment(sketch, "E205.1", {"start": v(0.02, -2.36) * mm, "end": v(4.26, -7.33) * mm});
            skLineSegment(sketch, "E205.2", {"start": v(0.02, -2.36) * mm, "end": v(-5.32, -8.61) * mm});
            skLineSegment(sketch, "E205.3", {"start": v(-5.32, -8.61) * mm, "end": v(-0.86, -14) * mm});
            skLineSegment(sketch, "E206", {"start": v(12.4, -16.1) * mm, "end": v(6.3, -23.41) * mm, "construction": true});
            skLineSegment(sketch, "E207.0", {"start": v(4.93, -8.12) * mm, "end": v(11.74, -16.1) * mm});
            skLineSegment(sketch, "E207.1", {"start": v(4.93, -8.12) * mm, "end": v(-0.2, -14.8) * mm});
            skLineSegment(sketch, "E207.2", {"start": v(-0.2, -14.8) * mm, "end": v(6.3, -22.62) * mm});
            skLineSegment(sketch, "E207.3", {"start": v(11.74, -16.1) * mm, "end": v(6.3, -22.62) * mm});
            skLineSegment(sketch, "E208.0", {"start": v(-6, -9.4) * mm, "end": v(-1.5, -14.82) * mm});
            skLineSegment(sketch, "E208.1", {"start": v(-6, -9.4) * mm, "end": v(-11.71, -16.1) * mm});
            skLineSegment(sketch, "E208.2", {"start": v(-11.71, -16.1) * mm, "end": v(-6.9, -21.87) * mm});
            skLineSegment(sketch, "E208.3", {"start": v(-1.5, -14.82) * mm, "end": v(-6.9, -21.87) * mm});
            skLineSegment(sketch, "E209", {"start": v(-0.02, -31) * mm, "end": v(-6.34, -38.6) * mm, "construction": true});
            skLineSegment(sketch, "E210", {"start": v(0, -30.97) * mm, "end": v(6.35, -38.6) * mm, "construction": true});
            skLineSegment(sketch, "E211.0", {"start": v(-0.83, -15.63) * mm, "end": v(-6.23, -22.67) * mm});
            skLineSegment(sketch, "E211.1", {"start": v(-0.83, -15.63) * mm, "end": v(5.63, -23.4) * mm});
            skLineSegment(sketch, "E211.2", {"start": v(5.63, -23.4) * mm, "end": v(0, -30.16) * mm});
            skLineSegment(sketch, "E211.3", {"start": v(-6.23, -22.67) * mm, "end": v(0, -30.16) * mm});
            skLineSegment(sketch, "E212", {"start": v(-12.97, -30.6) * mm, "end": v(-19.05, -38.52) * mm, "construction": true});
            skLineSegment(sketch, "E213", {"start": v(-12.98, -30.62) * mm, "end": v(-6.34, -38.6) * mm, "construction": true});
            skLineSegment(sketch, "E214", {"start": v(12.64, -31.04) * mm, "end": v(19.06, -38.77) * mm, "construction": true});
            skLineSegment(sketch, "E215", {"start": v(12.64, -31.04) * mm, "end": v(6.32, -38.63) * mm, "construction": true});
            skLineSegment(sketch, "E216", {"start": v(6.32, -38.63) * mm, "end": v(0, -46.22) * mm, "construction": true});
            skLineSegment(sketch, "E217", {"start": v(6.35, -38.6) * mm, "end": v(12.7, -46.22) * mm, "construction": true});
            skLineSegment(sketch, "E218.0", {"start": v(-6.87, -23.5) * mm, "end": v(-0.65, -30.97) * mm});
            skLineSegment(sketch, "E218.1", {"start": v(-6.87, -23.5) * mm, "end": v(-12.33, -30.6) * mm});
            skLineSegment(sketch, "E218.2", {"start": v(-12.33, -30.6) * mm, "end": v(-6.34, -37.8) * mm});
            skLineSegment(sketch, "E218.3", {"start": v(-0.65, -30.97) * mm, "end": v(-6.34, -37.8) * mm});
            skLineSegment(sketch, "E219.0", {"start": v(6.3, -24.2) * mm, "end": v(0.67, -30.97) * mm});
            skLineSegment(sketch, "E219.1", {"start": v(6.3, -24.2) * mm, "end": v(11.98, -31.04) * mm});
            skLineSegment(sketch, "E219.2", {"start": v(11.98, -31.04) * mm, "end": v(6.35, -37.8) * mm});
            skLineSegment(sketch, "E219.3", {"start": v(0.67, -30.97) * mm, "end": v(6.35, -37.8) * mm});
            skLineSegment(sketch, "E220.0", {"start": v(0, -31.76) * mm, "end": v(5.7, -38.6) * mm});
            skLineSegment(sketch, "E220.1", {"start": v(0, -31.76) * mm, "end": v(-5.68, -38.6) * mm});
            skLineSegment(sketch, "E220.2", {"start": v(-5.68, -38.6) * mm, "end": v(0, -45.42) * mm});
            skLineSegment(sketch, "E220.3", {"start": v(5.7, -38.6) * mm, "end": v(0, -45.42) * mm});
            skLineSegment(sketch, "E221.0", {"start": v(12.67, 25.94) * mm, "end": v(17.97, 20.25) * mm});
            skLineSegment(sketch, "E221.1", {"start": v(12.67, 25.94) * mm, "end": v(6.98, 19.48) * mm});
            skLineSegment(sketch, "E221.2", {"start": v(6.98, 19.48) * mm, "end": v(12.3, 13.6) * mm});
            skLineSegment(sketch, "E221.3", {"start": v(17.97, 20.25) * mm, "end": v(12.3, 13.6) * mm});
            skLineSegment(sketch, "E222", {"start": v(18.26, 6.25) * mm, "end": v(10.68, 0.2) * mm, "construction": true});
            skLineSegment(sketch, "E223.0", {"start": v(6.72, 5.49) * mm, "end": v(10.75, 0.9) * mm});
            skLineSegment(sketch, "E223.1", {"start": v(12.32, 12.04) * mm, "end": v(6.72, 5.49) * mm});
            skLineSegment(sketch, "E223.2", {"start": v(12.32, 12.04) * mm, "end": v(17.51, 6.3) * mm});
            skLineSegment(sketch, "E223.3", {"start": v(17.51, 6.3) * mm, "end": v(10.75, 0.9) * mm});
            skLineSegment(sketch, "E224", {"start": v(18.52, -8.7) * mm, "end": v(25.06, -16.14) * mm, "construction": true});
            skLineSegment(sketch, "E225.0", {"start": v(10.71, -0.6) * mm, "end": v(17.87, -8.74) * mm});
            skLineSegment(sketch, "E225.1", {"start": v(10.71, -0.6) * mm, "end": v(5.56, -7.3) * mm});
            skLineSegment(sketch, "E225.2", {"start": v(5.56, -7.3) * mm, "end": v(12.4, -15.3) * mm});
            skLineSegment(sketch, "E225.3", {"start": v(17.87, -8.74) * mm, "end": v(12.4, -15.3) * mm});
            skLineSegment(sketch, "E226", {"start": v(18.83, -23.63) * mm, "end": v(25.25, -31.16) * mm, "construction": true});
            skLineSegment(sketch, "E227.0", {"start": v(12.4, -16.88) * mm, "end": v(18.16, -23.63) * mm});
            skLineSegment(sketch, "E227.1", {"start": v(12.4, -16.88) * mm, "end": v(6.97, -23.41) * mm});
            skLineSegment(sketch, "E227.2", {"start": v(6.97, -23.41) * mm, "end": v(12.65, -30.25) * mm});
            skLineSegment(sketch, "E227.3", {"start": v(18.16, -23.63) * mm, "end": v(12.65, -30.25) * mm});
            skLineSegment(sketch, "E228.0", {"start": v(12.64, -31.84) * mm, "end": v(18.3, -38.64) * mm});
            skLineSegment(sketch, "E228.1", {"start": v(12.64, -31.84) * mm, "end": v(7.01, -38.6) * mm});
            skLineSegment(sketch, "E228.2", {"start": v(7.01, -38.6) * mm, "end": v(12.7, -45.42) * mm});
            skLineSegment(sketch, "E228.3", {"start": v(18.3, -38.64) * mm, "end": v(12.7, -45.42) * mm});
            skLineSegment(sketch, "E229.0", {"start": v(6.35, -39.39) * mm, "end": v(11.62, -45.7) * mm});
            skLineSegment(sketch, "E229.1", {"start": v(6.35, -39.39) * mm, "end": v(1.08, -45.7) * mm});
            skLineSegment(sketch, "E229.2", {"start": v(11.62, -45.7) * mm, "end": v(1.08, -45.7) * mm});
            skLineSegment(sketch, "E230", {"start": v(-18.53, -8.7) * mm, "end": v(-12.37, -16.1) * mm, "construction": true});
            skLineSegment(sketch, "E231.0", {"start": v(-12.53, 25.84) * mm, "end": v(-17.88, 20.19) * mm});
            skLineSegment(sketch, "E231.1", {"start": v(-12.53, 25.84) * mm, "end": v(-6.72, 19.24) * mm});
            skLineSegment(sketch, "E231.2", {"start": v(-6.72, 19.24) * mm, "end": v(-12.09, 13.4) * mm});
            skLineSegment(sketch, "E231.3", {"start": v(-17.88, 20.19) * mm, "end": v(-12.09, 13.4) * mm});
            skLineSegment(sketch, "E232.0", {"start": v(-12.12, 11.86) * mm, "end": v(-17.48, 6.02) * mm});
            skLineSegment(sketch, "E232.1", {"start": v(-12.12, 11.86) * mm, "end": v(-6.7, 5.5) * mm});
            skLineSegment(sketch, "E232.2", {"start": v(-6.7, 5.5) * mm, "end": v(-12.02, -0.55) * mm});
            skLineSegment(sketch, "E232.3", {"start": v(-17.48, 6.02) * mm, "end": v(-12.02, -0.55) * mm});
            skLineSegment(sketch, "E233.0", {"start": v(-12.04, -2.11) * mm, "end": v(-17.86, -8.71) * mm});
            skLineSegment(sketch, "E233.1", {"start": v(-12.04, -2.11) * mm, "end": v(-6.65, -8.6) * mm});
            skLineSegment(sketch, "E233.2", {"start": v(-6.65, -8.6) * mm, "end": v(-12.37, -15.3) * mm});
            skLineSegment(sketch, "E233.3", {"start": v(-17.86, -8.71) * mm, "end": v(-12.37, -15.3) * mm});
            skLineSegment(sketch, "E234.0", {"start": v(-12.38, -16.88) * mm, "end": v(-18.14, -23.62) * mm});
            skLineSegment(sketch, "E234.1", {"start": v(-12.38, -16.88) * mm, "end": v(-7.54, -22.7) * mm});
            skLineSegment(sketch, "E234.2", {"start": v(-7.54, -22.7) * mm, "end": v(-13, -29.8) * mm});
            skLineSegment(sketch, "E234.3", {"start": v(-18.14, -23.62) * mm, "end": v(-13, -29.8) * mm});
            skLineSegment(sketch, "E235.0", {"start": v(-12.55, -38.4) * mm, "end": v(-12.82, -38.75) * mm});
            skLineSegment(sketch, "E235.1", {"start": v(-13.08, -38.43) * mm, "end": v(-12.82, -38.75) * mm});
            skLineSegment(sketch, "E235.3", {"start": v(-12.7, -38.2) * mm, "end": v(-12.55, -38.4) * mm});
            skLineSegment(sketch, "E236.0", {"start": v(-25.06, 27.03) * mm, "end": v(-30.47, 21.67) * mm});
            skLineSegment(sketch, "E236.1", {"start": v(-25.06, 27.03) * mm, "end": v(-19.25, 20.22) * mm});
            skLineSegment(sketch, "E236.2", {"start": v(-19.25, 20.22) * mm, "end": v(-24.59, 14.58) * mm});
            skLineSegment(sketch, "E236.3", {"start": v(-30.47, 21.67) * mm, "end": v(-24.59, 14.58) * mm});
            skLineSegment(sketch, "E237.0", {"start": v(-24.64, 13.05) * mm, "end": v(-18.83, 6.06) * mm});
            skLineSegment(sketch, "E237.1", {"start": v(-24.64, 13.05) * mm, "end": v(-30.67, 6.68) * mm});
            skLineSegment(sketch, "E237.2", {"start": v(-30.67, 6.68) * mm, "end": v(-24.77, -0.4) * mm});
            skLineSegment(sketch, "E237.3", {"start": v(-18.83, 6.06) * mm, "end": v(-24.77, -0.4) * mm});
            skLineSegment(sketch, "E238", {"start": v(-18.53, -8.7) * mm, "end": v(-25.05, -16.11) * mm, "construction": true});
            skLineSegment(sketch, "E239.0", {"start": v(-24.8, -1.95) * mm, "end": v(-19.2, -8.7) * mm});
            skLineSegment(sketch, "E239.1", {"start": v(-24.8, -1.95) * mm, "end": v(-30.77, -8.44) * mm});
            skLineSegment(sketch, "E239.2", {"start": v(-30.77, -8.44) * mm, "end": v(-25.04, -15.33) * mm});
            skLineSegment(sketch, "E239.3", {"start": v(-19.2, -8.7) * mm, "end": v(-25.04, -15.33) * mm});
            skLineSegment(sketch, "E240.0", {"start": v(-25.08, -16.87) * mm, "end": v(-19.47, -23.61) * mm});
            skLineSegment(sketch, "E240.1", {"start": v(-25.08, -16.87) * mm, "end": v(-30.9, -23.5) * mm});
            skLineSegment(sketch, "E240.2", {"start": v(-30.9, -23.5) * mm, "end": v(-25.2, -30.34) * mm});
            skLineSegment(sketch, "E240.3", {"start": v(-19.47, -23.61) * mm, "end": v(-25.2, -30.34) * mm});
            skLineSegment(sketch, "E241.0", {"start": v(-25.22, -31.91) * mm, "end": v(-19.71, -38.52) * mm});
            skLineSegment(sketch, "E241.1", {"start": v(-25.22, -31.91) * mm, "end": v(-31, -38.68) * mm});
            skLineSegment(sketch, "E241.2", {"start": v(-31, -38.68) * mm, "end": v(-25.4, -45.42) * mm});
            skLineSegment(sketch, "E241.3", {"start": v(-19.71, -38.52) * mm, "end": v(-25.4, -45.42) * mm});
            skLineSegment(sketch, "E242", {"start": v(18.67, 20.27) * mm, "end": v(24.67, 13.94) * mm, "construction": true});
            skLineSegment(sketch, "E243.0", {"start": v(25.09, 27) * mm, "end": v(30.46, 21.65) * mm});
            skLineSegment(sketch, "E243.1", {"start": v(25.09, 27) * mm, "end": v(19.35, 20.28) * mm});
            skLineSegment(sketch, "E243.2", {"start": v(19.35, 20.28) * mm, "end": v(24.64, 14.7) * mm});
            skLineSegment(sketch, "E243.3", {"start": v(30.46, 21.65) * mm, "end": v(24.64, 14.7) * mm});
            skLineSegment(sketch, "E244", {"start": v(18.3, 6.2) * mm, "end": v(24.89, -1.11) * mm, "construction": true});
            skLineSegment(sketch, "E245", {"start": v(18.26, 6.25) * mm, "end": v(24.67, 13.94) * mm, "construction": true});
            skLineSegment(sketch, "E246.0", {"start": v(18.92, 6.25) * mm, "end": v(24.65, 13.13) * mm});
            skLineSegment(sketch, "E246.1", {"start": v(18.92, 6.25) * mm, "end": v(24.87, -0.34) * mm});
            skLineSegment(sketch, "E246.2", {"start": v(30.7, 6.66) * mm, "end": v(24.87, -0.34) * mm});
            skLineSegment(sketch, "E246.3", {"start": v(24.65, 13.13) * mm, "end": v(30.7, 6.66) * mm});
            skLineSegment(sketch, "E247.0", {"start": v(24.9, -1.9) * mm, "end": v(19.2, -8.72) * mm});
            skLineSegment(sketch, "E247.1", {"start": v(24.9, -1.9) * mm, "end": v(30.81, -8.45) * mm});
            skLineSegment(sketch, "E247.2", {"start": v(30.81, -8.45) * mm, "end": v(25.05, -15.36) * mm});
            skLineSegment(sketch, "E247.3", {"start": v(19.2, -8.72) * mm, "end": v(25.05, -15.36) * mm});
            skLineSegment(sketch, "E248.0", {"start": v(25.07, -16.93) * mm, "end": v(19.5, -23.62) * mm});
            skLineSegment(sketch, "E248.1", {"start": v(25.07, -16.93) * mm, "end": v(30.91, -23.57) * mm});
            skLineSegment(sketch, "E248.2", {"start": v(30.91, -23.57) * mm, "end": v(25.25, -30.37) * mm});
            skLineSegment(sketch, "E248.3", {"start": v(19.5, -23.62) * mm, "end": v(25.25, -30.37) * mm});
            skLineSegment(sketch, "E249", {"start": v(18.95, -38.64) * mm, "end": v(25.4, -46.22) * mm, "construction": true});
            skLineSegment(sketch, "E250", {"start": v(19.06, -38.77) * mm, "end": v(25.25, -31.16) * mm, "construction": true});
            skLineSegment(sketch, "E251.0", {"start": v(19.72, -38.76) * mm, "end": v(25.26, -31.95) * mm});
            skLineSegment(sketch, "E251.1", {"start": v(19.72, -38.76) * mm, "end": v(25.4, -45.43) * mm});
            skLineSegment(sketch, "E251.2", {"start": v(31.01, -38.7) * mm, "end": v(25.4, -45.43) * mm});
            skLineSegment(sketch, "E251.3", {"start": v(25.26, -31.95) * mm, "end": v(31.01, -38.7) * mm});
            skLineSegment(sketch, "E252.0", {"start": v(-12.96, -31.43) * mm, "end": v(-18.4, -38.5) * mm});
            skLineSegment(sketch, "E252.1", {"start": v(-12.96, -31.43) * mm, "end": v(-7, -38.6) * mm});
            skLineSegment(sketch, "E252.2", {"start": v(-7, -38.6) * mm, "end": v(-12.67, -45.39) * mm});
            skLineSegment(sketch, "E252.3", {"start": v(-18.4, -38.5) * mm, "end": v(-12.67, -45.39) * mm});
            skLineSegment(sketch, "E253", {"start": v(19.06, -38.77) * mm, "end": v(12.7, -46.22) * mm, "construction": true});
            skLineSegment(sketch, "E254", {"start": v(18.94, 33.85) * mm, "end": v(18.67, 20.27) * mm, "construction": true});
            skLineSegment(sketch, "E255", {"start": v(18.67, 20.27) * mm, "end": v(18.26, 6.25) * mm, "construction": true});
            skLineSegment(sketch, "E256", {"start": v(18.3, 6.2) * mm, "end": v(18.54, -8.73) * mm, "construction": true});
            skLineSegment(sketch, "E257", {"start": v(18.52, -8.7) * mm, "end": v(18.83, -23.63) * mm, "construction": true});
            skLineSegment(sketch, "E258", {"start": v(18.83, -23.63) * mm, "end": v(19.06, -38.77) * mm, "construction": true});
            skLineSegment(sketch, "E259", {"start": v(18.95, -38.64) * mm, "end": v(18.98, -46.22) * mm, "construction": true});
            skLineSegment(sketch, "E260", {"start": v(-18.9, 33.86) * mm, "end": v(-18.57, 20.2) * mm, "construction": true});
            skLineSegment(sketch, "E261", {"start": v(-18.57, 20.2) * mm, "end": v(-18.15, 6.04) * mm, "construction": true});
            skLineSegment(sketch, "E262", {"start": v(-18.15, 6.04) * mm, "end": v(-18.53, -8.7) * mm, "construction": true});
            skLineSegment(sketch, "E263", {"start": v(-18.53, -8.7) * mm, "end": v(-18.8, -23.62) * mm, "construction": true});
            skLineSegment(sketch, "E264", {"start": v(-18.8, -23.62) * mm, "end": v(-19.19, -38.36) * mm, "construction": true});
            skLineSegment(sketch, "E265", {"start": v(-19.05, -38.52) * mm, "end": v(-19.02, -46.22) * mm, "construction": true});
            skLineSegment(sketch, "E266.0", {"start": v(19.42, 32.65) * mm, "end": v(19.2, 21.68) * mm});
            skLineSegment(sketch, "E266.1", {"start": v(19.42, 32.65) * mm, "end": v(24.37, 27.72) * mm});
            skLineSegment(sketch, "E266.2", {"start": v(24.37, 27.72) * mm, "end": v(19.2, 21.68) * mm});
            skLineSegment(sketch, "E267.0", {"start": v(18.4, 32.47) * mm, "end": v(18.19, 21.53) * mm});
            skLineSegment(sketch, "E267.1", {"start": v(18.4, 32.47) * mm, "end": v(13.34, 26.72) * mm});
            skLineSegment(sketch, "E267.2", {"start": v(13.34, 26.72) * mm, "end": v(18.19, 21.53) * mm});
            skLineSegment(sketch, "E268.0", {"start": v(19.14, 19.03) * mm, "end": v(18.81, 7.7) * mm});
            skLineSegment(sketch, "E268.1", {"start": v(19.14, 19.03) * mm, "end": v(23.99, 13.92) * mm});
            skLineSegment(sketch, "E268.2", {"start": v(18.81, 7.7) * mm, "end": v(23.99, 13.92) * mm});
            skLineSegment(sketch, "E269.0", {"start": v(18.12, 18.84) * mm, "end": v(17.8, 7.5) * mm});
            skLineSegment(sketch, "E269.1", {"start": v(18.12, 18.84) * mm, "end": v(12.98, 12.82) * mm});
            skLineSegment(sketch, "E269.2", {"start": v(12.98, 12.82) * mm, "end": v(17.8, 7.5) * mm});
            skLineSegment(sketch, "E270.0", {"start": v(17.8, 5.24) * mm, "end": v(11.42, 0.14) * mm});
            skLineSegment(sketch, "E270.1", {"start": v(17.8, 5.24) * mm, "end": v(18.01, -7.35) * mm});
            skLineSegment(sketch, "E270.2", {"start": v(11.42, 0.14) * mm, "end": v(18.01, -7.35) * mm});
            skLineSegment(sketch, "E271.0", {"start": v(18.83, 4.84) * mm, "end": v(19.03, -7.35) * mm});
            skLineSegment(sketch, "E271.1", {"start": v(18.83, 4.84) * mm, "end": v(24.21, -1.13) * mm});
            skLineSegment(sketch, "E271.2", {"start": v(24.21, -1.13) * mm, "end": v(19.03, -7.35) * mm});
            skLineSegment(sketch, "E272.0", {"start": v(18.04, -10.12) * mm, "end": v(13.07, -16.1) * mm});
            skLineSegment(sketch, "E272.1", {"start": v(18.04, -10.12) * mm, "end": v(18.29, -22.21) * mm});
            skLineSegment(sketch, "E272.2", {"start": v(13.07, -16.1) * mm, "end": v(18.29, -22.21) * mm});
            skLineSegment(sketch, "E273.0", {"start": v(19.06, -10.09) * mm, "end": v(19.3, -22.26) * mm});
            skLineSegment(sketch, "E273.1", {"start": v(19.06, -10.09) * mm, "end": v(24.4, -16.15) * mm});
            skLineSegment(sketch, "E273.2", {"start": v(24.4, -16.15) * mm, "end": v(19.3, -22.26) * mm});
            skLineSegment(sketch, "E274.0", {"start": v(18.35, -24.98) * mm, "end": v(18.54, -37.36) * mm});
            skLineSegment(sketch, "E274.1", {"start": v(18.35, -24.98) * mm, "end": v(13.3, -31.04) * mm});
            skLineSegment(sketch, "E274.2", {"start": v(13.3, -31.04) * mm, "end": v(18.54, -37.36) * mm});
            skLineSegment(sketch, "E275.0", {"start": v(19.36, -25.05) * mm, "end": v(19.55, -37.35) * mm});
            skLineSegment(sketch, "E275.1", {"start": v(19.36, -25.05) * mm, "end": v(24.58, -31.16) * mm});
            skLineSegment(sketch, "E275.2", {"start": v(19.55, -37.35) * mm, "end": v(24.58, -31.16) * mm});
            skLineSegment(sketch, "E276.0", {"start": v(18.46, -40.25) * mm, "end": v(18.48, -45.71) * mm});
            skLineSegment(sketch, "E276.1", {"start": v(18.46, -40.25) * mm, "end": v(13.8, -45.71) * mm});
            skLineSegment(sketch, "E276.2", {"start": v(18.48, -45.71) * mm, "end": v(13.8, -45.71) * mm});
            skLineSegment(sketch, "E277.0", {"start": v(19.46, -40.01) * mm, "end": v(19.48, -45.71) * mm});
            skLineSegment(sketch, "E277.1", {"start": v(19.46, -40.01) * mm, "end": v(24.31, -45.71) * mm});
            skLineSegment(sketch, "E277.2", {"start": v(24.31, -45.71) * mm, "end": v(19.48, -45.71) * mm});
            skLineSegment(sketch, "E278.0", {"start": v(-19.38, 32.64) * mm, "end": v(-19.12, 21.65) * mm});
            skLineSegment(sketch, "E278.1", {"start": v(-19.38, 32.64) * mm, "end": v(-24.32, 27.75) * mm});
            skLineSegment(sketch, "E278.2", {"start": v(-24.32, 27.75) * mm, "end": v(-19.12, 21.65) * mm});
            skLineSegment(sketch, "E279.0", {"start": v(-18.35, 32.47) * mm, "end": v(-18.09, 21.45) * mm});
            skLineSegment(sketch, "E279.1", {"start": v(-18.35, 32.47) * mm, "end": v(-13.2, 26.6) * mm});
            skLineSegment(sketch, "E279.2", {"start": v(-13.2, 26.6) * mm, "end": v(-18.09, 21.45) * mm});
            skLineSegment(sketch, "E280.0", {"start": v(-19.03, 18.98) * mm, "end": v(-23.94, 13.8) * mm});
            skLineSegment(sketch, "E280.1", {"start": v(-19.03, 18.98) * mm, "end": v(-18.7, 7.49) * mm});
            skLineSegment(sketch, "E280.2", {"start": v(-23.94, 13.8) * mm, "end": v(-18.7, 7.49) * mm});
            skLineSegment(sketch, "E281.0", {"start": v(-18.01, 18.77) * mm, "end": v(-17.68, 7.31) * mm});
            skLineSegment(sketch, "E281.1", {"start": v(-18.01, 18.77) * mm, "end": v(-12.78, 12.64) * mm});
            skLineSegment(sketch, "E281.2", {"start": v(-12.78, 12.64) * mm, "end": v(-17.68, 7.31) * mm});
            skLineSegment(sketch, "E282.0", {"start": v(-18.69, 4.73) * mm, "end": v(-18.99, -7.36) * mm});
            skLineSegment(sketch, "E282.1", {"start": v(-18.69, 4.73) * mm, "end": v(-24.13, -1.2) * mm});
            skLineSegment(sketch, "E282.2", {"start": v(-24.13, -1.2) * mm, "end": v(-18.99, -7.36) * mm});
            skLineSegment(sketch, "E283.0", {"start": v(-17.68, 4.68) * mm, "end": v(-17.98, -7.32) * mm});
            skLineSegment(sketch, "E283.1", {"start": v(-17.68, 4.68) * mm, "end": v(-12.7, -1.32) * mm});
            skLineSegment(sketch, "E283.2", {"start": v(-12.7, -1.32) * mm, "end": v(-17.98, -7.32) * mm});
            skLineSegment(sketch, "E284.0", {"start": v(-19.05, -10.05) * mm, "end": v(-24.4, -16.12) * mm});
            skLineSegment(sketch, "E284.1", {"start": v(-19.05, -10.05) * mm, "end": v(-19.28, -22.27) * mm});
            skLineSegment(sketch, "E284.2", {"start": v(-24.4, -16.12) * mm, "end": v(-19.28, -22.27) * mm});
            skLineSegment(sketch, "E285.0", {"start": v(-19.35, -25.04) * mm, "end": v(-24.55, -31.13) * mm});
            skLineSegment(sketch, "E285.1", {"start": v(-19.35, -25.04) * mm, "end": v(-19.66, -37) * mm});
            skLineSegment(sketch, "E285.2", {"start": v(-24.55, -31.13) * mm, "end": v(-19.66, -37) * mm});
            skLineSegment(sketch, "E286.0", {"start": v(-18.33, -24.98) * mm, "end": v(-18.65, -37.17) * mm});
            skLineSegment(sketch, "E286.1", {"start": v(-18.33, -24.98) * mm, "end": v(-13.63, -30.63) * mm});
            skLineSegment(sketch, "E286.2", {"start": v(-13.63, -30.63) * mm, "end": v(-18.65, -37.17) * mm});
            skLineSegment(sketch, "E287.0", {"start": v(-19.55, -39.93) * mm, "end": v(-24.32, -45.7) * mm});
            skLineSegment(sketch, "E287.1", {"start": v(-19.55, -39.93) * mm, "end": v(-19.53, -45.7) * mm});
            skLineSegment(sketch, "E287.2", {"start": v(-19.53, -45.7) * mm, "end": v(-24.32, -45.7) * mm});
            skLineSegment(sketch, "E288.0", {"start": v(-18.54, -39.92) * mm, "end": v(-18.52, -45.71) * mm});
            skLineSegment(sketch, "E288.1", {"start": v(-18.54, -39.92) * mm, "end": v(-13.72, -45.71) * mm});
            skLineSegment(sketch, "E288.2", {"start": v(-13.72, -45.71) * mm, "end": v(-18.52, -45.71) * mm});
            skLineSegment(sketch, "E289.0", {"start": v(-18.05, -10.05) * mm, "end": v(-13.03, -16.09) * mm});
            skLineSegment(sketch, "E289.1", {"start": v(-18.05, -10.05) * mm, "end": v(-18.28, -22.23) * mm});
            skLineSegment(sketch, "E289.2", {"start": v(-13.03, -16.09) * mm, "end": v(-18.28, -22.23) * mm});
            skLineSegment(sketch, "E290", {"start": v(-38.1, 30.06) * mm, "end": v(-19.02, 46.83) * mm});
            skLineSegment(sketch, "E291", {"start": v(-38.1, 30.06) * mm, "end": v(-38.1, 72.44) * mm});
            skLineSegment(sketch, "E292", {"start": v(38.1, 29.98) * mm, "end": v(38.1, 74.77) * mm});
            skLineSegment(sketch, "E293", {"start": v(38.1, 74.77) * mm, "end": v(-37.89, 74.77) * mm});
            skLineSegment(sketch, "E294", {"start": v(-37.89, 74.77) * mm, "end": v(-38.1, 72.44) * mm});
            skLineSegment(sketch, "E295", {"start": v(-19.02, 46.83) * mm, "end": v(-12.48, 40.22) * mm});
            skLineSegment(sketch, "E296", {"start": v(-12.48, 40.22) * mm, "end": v(12.92, 39.85) * mm});
            skLineSegment(sketch, "E297", {"start": v(12.92, 39.85) * mm, "end": v(19.08, 46.82) * mm});
            skLineSegment(sketch, "E298", {"start": v(19.08, 46.82) * mm, "end": v(38.1, 29.98) * mm});
            skPoint(sketch, "E299", {"position": v(0.02, -1.58) * mm});
            skLineSegment(sketch, "E300", {"start": v(-20, 45.97) * mm, "end": v(-18.18, 45.97) * mm});
            skLineSegment(sketch, "E301", {"start": v(18.28, 45.91) * mm, "end": v(20.1, 45.91) * mm});
            skLineSegment(sketch, "E302", {"start": v(-20, 45.97) * mm, "end": v(-20, 55.2) * mm});
            skLineSegment(sketch, "E303", {"start": v(-20, 55.2) * mm, "end": v(-20, 45.97) * mm});
            skLineSegment(sketch, "E304", {"start": v(-18.18, 45.97) * mm, "end": v(-18.18, 55) * mm});
            skLineSegment(sketch, "E305", {"start": v(18.28, 45.91) * mm, "end": v(18.28, 55.53) * mm});
            skLineSegment(sketch, "E306", {"start": v(20.1, 45.91) * mm, "end": v(20.1, 55.4) * mm});
            skPoint(sketch, "E307.startSnap0", {"position": v(3.37, 9.3) * mm});
            skLineSegment(sketch, "E308", {"start": v(-3.5, 36.86) * mm, "end": v(3.88, 36.86) * mm});
            skPoint(sketch, "E308.startSnap0", {"position": v(-8.75, 36.86) * mm});
            skLineSegment(sketch, "E309", {"start": v(-3.5, 36.86) * mm, "end": v(-1.74, 40.07) * mm});
            skLineSegment(sketch, "E310", {"start": v(3.88, 36.86) * mm, "end": v(2.02, 40.01) * mm});
            skLineSegment(sketch, "E311", {"start": v(-3.5, 36.86) * mm, "end": v(-1.74, 35.2) * mm});
            skLineSegment(sketch, "E312", {"start": v(3.88, 36.86) * mm, "end": v(2.12, 35.2) * mm});
            skLineSegment(sketch, "E313", {"start": v(-1.74, 35.2) * mm, "end": v(-1.74, 30.6) * mm});
            skLineSegment(sketch, "E314", {"start": v(2.12, 35.2) * mm, "end": v(2.12, 30.6) * mm});
            skLineSegment(sketch, "E315", {"start": v(-1.74, 30.6) * mm, "end": v(-3.24, 29.25) * mm});
            skLineSegment(sketch, "E316", {"start": v(2.12, 30.6) * mm, "end": v(3.84, 29.22) * mm});
            skLineSegment(sketch, "E317", {"start": v(-3.24, 29.25) * mm, "end": v(-4.76, 27.87) * mm});
            skLineSegment(sketch, "E318", {"start": v(0.29, 26.86) * mm, "end": v(0.29, 29.54) * mm});
            skLineSegment(sketch, "E319", {"start": v(-4.76, 27.87) * mm, "end": v(0.29, 27.87) * mm});
            skLineSegment(sketch, "E320", {"start": v(0.29, 27.87) * mm, "end": v(5.34, 27.87) * mm});
            skLineSegment(sketch, "E321", {"start": v(5.34, 27.87) * mm, "end": v(3.84, 29.22) * mm});
            skLineSegment(sketch, "E322", {"start": v(0.28, 25.35) * mm, "end": v(0.28, 22.48) * mm});
            skLineSegment(sketch, "E323", {"start": v(-4.76, 27.87) * mm, "end": v(0.28, 22.48) * mm});
            skLineSegment(sketch, "E324", {"start": v(5.34, 27.87) * mm, "end": v(0.28, 22.48) * mm});
            skLineSegment(sketch, "E325", {"start": v(-1.05, 23.9) * mm, "end": v(-1.05, 16.17) * mm});
            skPoint(sketch, "E325.endSnap0", {"position": v(-2.67, 16.17) * mm});
            skLineSegment(sketch, "E326", {"start": v(-1.05, 16.17) * mm, "end": v(1.6, 16.17) * mm});
            skLineSegment(sketch, "E327", {"start": v(1.6, 23.9) * mm, "end": v(1.6, 16.17) * mm});
            skLineSegment(sketch, "E328", {"start": v(-1.05, 16.17) * mm, "end": v(-3.28, 14.21) * mm});
            skLineSegment(sketch, "E329", {"start": v(1.6, 16.17) * mm, "end": v(3.83, 14.21) * mm});
            skLineSegment(sketch, "E330", {"start": v(-3.28, 14.21) * mm, "end": v(-3.28, 13.2) * mm});
            skLineSegment(sketch, "E331", {"start": v(-3.28, 13.2) * mm, "end": v(3.83, 13.2) * mm});
            skLineSegment(sketch, "E332", {"start": v(3.83, 14.21) * mm, "end": v(3.83, 13.2) * mm});
            skPoint(sketch, "E333.orphan", {"position": v(2.07, 16.17) * mm});
            skPoint(sketch, "E307.start.orphan", {"position": v(-2, 9.3) * mm});
            skLineSegment(sketch, "E334.trimOffspring", {"start": v(2.02, 13.2) * mm, "end": v(2.02, 15.4) * mm});
            skLineSegment(sketch, "E335", {"start": v(-1.74, 40.07) * mm, "end": v(-1.74, 54.34) * mm});
            skLineSegment(sketch, "E336", {"start": v(-1.74, 54.34) * mm, "end": v(2.2, 54.29) * mm});
            skLineSegment(sketch, "E337", {"start": v(2.2, 54.29) * mm, "end": v(2.02, 40.01) * mm});
            skLineSegment(sketch, "E338", {"start": v(-18.18, 54.31) * mm, "end": v(-20, 54.31) * mm});
            skPoint(sketch, "E338.startSnap0", {"position": v(0.23, 54.31) * mm});
            skLineSegment(sketch, "E339", {"start": v(18.28, 54.29) * mm, "end": v(20.1, 54.29) * mm});
            skLineSegment(sketch, "E340", {"start": v(-3.28, 13.2) * mm, "end": v(-6.01, 6.28) * mm});
            skLineSegment(sketch, "E341", {"start": v(3.83, 13.2) * mm, "end": v(6.04, 6.26) * mm});
            skSolve(sketch);
        }
        {
            var Q0;
            {var subQ0=sQuery(id+"F0.wireOp",EDGE,"E9");Q0=makeQuery(id+"F0.imprint","IMPRINT",FACE,{"disambiguationData":[TD([[makeQuery(id+"F0.imprint","IMPRINT",EDGE,{"derivedFrom":subQ0}),1.0]])]});}
            var Q1;
            {var subQ3=sQuery(id+"F0.wireOp",EDGE,"E9");Q1=makeQuery(id+"F0.imprint","IMPRINT",FACE,{"disambiguationData":[TD([[makeQuery(id+"F0.imprint","IMPRINT",EDGE,{"derivedFrom":subQ3}),-1.0]])]});}
            var Q2;
            {var subQ0=sQuery(id+"F0.wireOp",EDGE,"E5");var subQ1=sQuery(id+"F0.wireOp",EDGE,"E1");var subQ2=makeQuery(id+"F0.imprint","INTERSECT",VERTEX,{"derivedFrom":[subQ1,subQ0]});Q2=makeQuery(id+"F0.imprint","IMPRINT",FACE,{"disambiguationData":[TD([[makeQuery(id+"F0.imprint","IMPRINT",EDGE,{"disambiguationData":[TD([[subQ2,-1.0]])],"derivedFrom":subQ0}),-1.0]])]});}
            var Q3;
            {var subQ0=sQuery(id+"F0.wireOp",EDGE,"E3");var subQ1=sQuery(id+"F0.wireOp",EDGE,"E1");var subQ2=makeQuery(id+"F0.imprint","INTERSECT",VERTEX,{"derivedFrom":[subQ1,subQ0]});Q3=makeQuery(id+"F0.imprint","IMPRINT",FACE,{"disambiguationData":[TD([[makeQuery(id+"F0.imprint","IMPRINT",EDGE,{"disambiguationData":[TD([[subQ2,-1.0]])],"derivedFrom":subQ1}),-1.0]])]});}
            extrude(context, id + "F2", {"entities" : qUnion([Q0, Q1, Q2, Q3]), "endBound" : BoundingType.SYMMETRIC, "depth" : 100.53 * mm, "offsetDistance" : 25.4 * mm});
        }
        {
            var Q0;
            Q0=makeQuery(id+"F1.imprint","IMPRINT",FACE,{"disambiguationData":[TD([[makeQuery(id+"F1.imprint","IMPRINT",EDGE,{"derivedFrom":sQuery(id+"F1.wireOp",EDGE,"E273.0")}),1.0]])]});
            var Q1;
            Q1=makeQuery(id+"F1.imprint","IMPRINT",FACE,{"disambiguationData":[TD([[makeQuery(id+"F1.imprint","IMPRINT",EDGE,{"derivedFrom":sQuery(id+"F1.wireOp",EDGE,"E239.0")}),-1.0]])]});
            var Q2;
            Q2=makeQuery(id+"F1.imprint","IMPRINT",FACE,{"disambiguationData":[TD([[makeQuery(id+"F1.imprint","IMPRINT",EDGE,{"derivedFrom":sQuery(id+"F1.wireOp",EDGE,"E168.0")}),1.0]])]});
            var Q3;
            Q3=makeQuery(id+"F1.imprint","IMPRINT",FACE,{"disambiguationData":[TD([[makeQuery(id+"F1.imprint","IMPRINT",EDGE,{"derivedFrom":sQuery(id+"F1.wireOp",EDGE,"E220.0")}),-1.0]])]});
            var Q4;
            Q4=makeQuery(id+"F1.imprint","IMPRINT",FACE,{"disambiguationData":[TD([[makeQuery(id+"F1.imprint","IMPRINT",EDGE,{"derivedFrom":sQuery(id+"F1.wireOp",EDGE,"E218.0")}),-1.0]])]});
            var Q5;
            Q5=makeQuery(id+"F1.imprint","IMPRINT",FACE,{"disambiguationData":[TD([[makeQuery(id+"F1.imprint","IMPRINT",EDGE,{"derivedFrom":sQuery(id+"F1.wireOp",EDGE,"E73.0")}),1.0]])]});
            var Q6;
            Q6=makeQuery(id+"F1.imprint","IMPRINT",FACE,{"disambiguationData":[TD([[makeQuery(id+"F1.imprint","IMPRINT",EDGE,{"derivedFrom":sQuery(id+"F1.wireOp",EDGE,"E272.0")}),1.0]])]});
            var Q7;
            Q7=makeQuery(id+"F1.imprint","IMPRINT",FACE,{"disambiguationData":[TD([[makeQuery(id+"F1.imprint","IMPRINT",EDGE,{"derivedFrom":sQuery(id+"F1.wireOp",EDGE,"E282.0")}),-1.0]])]});
            var Q8;
            Q8=makeQuery(id+"F1.imprint","IMPRINT",FACE,{"disambiguationData":[TD([[makeQuery(id+"F1.imprint","IMPRINT",EDGE,{"derivedFrom":sQuery(id+"F1.wireOp",EDGE,"E240.0")}),-1.0]])]});
            var Q9;
            Q9=makeQuery(id+"F1.imprint","IMPRINT",FACE,{"disambiguationData":[TD([[makeQuery(id+"F1.imprint","IMPRINT",EDGE,{"derivedFrom":sQuery(id+"F1.wireOp",EDGE,"E278.0")}),-1.0]])]});
            var Q10;
            Q10=makeQuery(id+"F1.imprint","IMPRINT",FACE,{"disambiguationData":[TD([[makeQuery(id+"F1.imprint","IMPRINT",EDGE,{"derivedFrom":sQuery(id+"F1.wireOp",EDGE,"E147.0")}),-1.0]])]});
            var Q11;
            Q11=makeQuery(id+"F1.imprint","IMPRINT",FACE,{"disambiguationData":[TD([[makeQuery(id+"F1.imprint","IMPRINT",EDGE,{"derivedFrom":sQuery(id+"F1.wireOp",EDGE,"E289.0")}),-1.0]])]});
            var Q12;
            Q12=makeQuery(id+"F1.imprint","IMPRINT",FACE,{"disambiguationData":[TD([[makeQuery(id+"F1.imprint","IMPRINT",EDGE,{"derivedFrom":sQuery(id+"F1.wireOp",EDGE,"E266.0")}),1.0]])]});
            var Q13;
            Q13=makeQuery(id+"F1.imprint","IMPRINT",FACE,{"disambiguationData":[TD([[makeQuery(id+"F1.imprint","IMPRINT",EDGE,{"derivedFrom":sQuery(id+"F1.wireOp",EDGE,"E281.0")}),1.0]])]});
            var Q14;
            Q14=makeQuery(id+"F1.imprint","IMPRINT",FACE,{"disambiguationData":[TD([[makeQuery(id+"F1.imprint","IMPRINT",EDGE,{"derivedFrom":sQuery(id+"F1.wireOp",EDGE,"E270.0")}),1.0]])]});
            var Q15;
            Q15=makeQuery(id+"F1.imprint","IMPRINT",FACE,{"disambiguationData":[TD([[makeQuery(id+"F1.imprint","IMPRINT",EDGE,{"derivedFrom":sQuery(id+"F1.wireOp",EDGE,"E140.0")}),-1.0]])]});
            var Q16;
            Q16=makeQuery(id+"F1.imprint","IMPRINT",FACE,{"disambiguationData":[TD([[makeQuery(id+"F1.imprint","IMPRINT",EDGE,{"derivedFrom":sQuery(id+"F1.wireOp",EDGE,"E167.0")}),1.0]])]});
            var Q17;
            Q17=makeQuery(id+"F1.imprint","IMPRINT",FACE,{"disambiguationData":[TD([[makeQuery(id+"F1.imprint","IMPRINT",EDGE,{"derivedFrom":sQuery(id+"F1.wireOp",EDGE,"E228.0")}),-1.0]])]});
            var Q18;
            Q18=makeQuery(id+"F1.imprint","IMPRINT",FACE,{"disambiguationData":[TD([[makeQuery(id+"F1.imprint","IMPRINT",EDGE,{"derivedFrom":sQuery(id+"F1.wireOp",EDGE,"E139.0")}),-1.0]])]});
            var Q19;
            Q19=makeQuery(id+"F1.imprint","IMPRINT",FACE,{"disambiguationData":[TD([[makeQuery(id+"F1.imprint","IMPRINT",EDGE,{"derivedFrom":sQuery(id+"F1.wireOp",EDGE,"E181.0")}),1.0]])]});
            var Q20;
            Q20=makeQuery(id+"F1.imprint","IMPRINT",FACE,{"disambiguationData":[TD([[makeQuery(id+"F1.imprint","IMPRINT",EDGE,{"derivedFrom":sQuery(id+"F1.wireOp",EDGE,"E277.0")}),1.0]])]});
            var Q21;
            Q21=makeQuery(id+"F1.imprint","IMPRINT",FACE,{"disambiguationData":[TD([[makeQuery(id+"F1.imprint","IMPRINT",EDGE,{"derivedFrom":sQuery(id+"F1.wireOp",EDGE,"E143.0")}),1.0]])]});
            var Q22;
            Q22=makeQuery(id+"F1.imprint","IMPRINT",FACE,{"disambiguationData":[TD([[makeQuery(id+"F1.imprint","IMPRINT",EDGE,{"derivedFrom":sQuery(id+"F1.wireOp",EDGE,"E208.0")}),-1.0]])]});
            var Q23;
            Q23=makeQuery(id+"F1.imprint","IMPRINT",FACE,{"disambiguationData":[TD([[makeQuery(id+"F1.imprint","IMPRINT",EDGE,{"derivedFrom":sQuery(id+"F1.wireOp",EDGE,"E207.0")}),-1.0]])]});
            var Q24;
            Q24=makeQuery(id+"F1.imprint","IMPRINT",FACE,{"disambiguationData":[TD([[makeQuery(id+"F1.imprint","IMPRINT",EDGE,{"derivedFrom":sQuery(id+"F1.wireOp",EDGE,"E268.0")}),1.0]])]});
            var Q25;
            Q25=makeQuery(id+"F1.imprint","IMPRINT",FACE,{"disambiguationData":[TD([[makeQuery(id+"F1.imprint","IMPRINT",EDGE,{"derivedFrom":sQuery(id+"F1.wireOp",EDGE,"E232.0")}),1.0]])]});
            var Q26;
            Q26=makeQuery(id+"F1.imprint","IMPRINT",FACE,{"disambiguationData":[TD([[makeQuery(id+"F1.imprint","IMPRINT",EDGE,{"derivedFrom":sQuery(id+"F1.wireOp",EDGE,"E283.0")}),1.0]])]});
            var Q27;
            Q27=makeQuery(id+"F1.imprint","IMPRINT",FACE,{"disambiguationData":[TD([[makeQuery(id+"F1.imprint","IMPRINT",EDGE,{"derivedFrom":sQuery(id+"F1.wireOp",EDGE,"E223.0")}),1.0]])]});
            var Q28;
            Q28=makeQuery(id+"F1.imprint","IMPRINT",FACE,{"disambiguationData":[TD([[makeQuery(id+"F1.imprint","IMPRINT",EDGE,{"derivedFrom":sQuery(id+"F1.wireOp",EDGE,"E158.0")}),-1.0]])]});
            var Q29;
            Q29=makeQuery(id+"F1.imprint","IMPRINT",FACE,{"disambiguationData":[TD([[makeQuery(id+"F1.imprint","IMPRINT",EDGE,{"derivedFrom":sQuery(id+"F1.wireOp",EDGE,"E236.0")}),1.0]])]});
            var Q30;
            Q30=makeQuery(id+"F1.imprint","IMPRINT",FACE,{"disambiguationData":[TD([[makeQuery(id+"F1.imprint","IMPRINT",EDGE,{"derivedFrom":sQuery(id+"F1.wireOp",EDGE,"E274.0")}),-1.0]])]});
            var Q31;
            Q31=makeQuery(id+"F1.imprint","IMPRINT",FACE,{"disambiguationData":[TD([[makeQuery(id+"F1.imprint","IMPRINT",EDGE,{"derivedFrom":sQuery(id+"F1.wireOp",EDGE,"E117.0")}),-1.0]])]});
            var Q32;
            Q32=makeQuery(id+"F1.imprint","IMPRINT",FACE,{"disambiguationData":[TD([[makeQuery(id+"F1.imprint","IMPRINT",EDGE,{"derivedFrom":sQuery(id+"F1.wireOp",EDGE,"E231.0")}),1.0]])]});
            var Q33;
            Q33=makeQuery(id+"F1.imprint","IMPRINT",FACE,{"disambiguationData":[TD([[makeQuery(id+"F1.imprint","IMPRINT",EDGE,{"derivedFrom":sQuery(id+"F1.wireOp",EDGE,"E115.0")}),-1.0]])]});
            var Q34;
            Q34=makeQuery(id+"F1.imprint","IMPRINT",FACE,{"disambiguationData":[TD([[makeQuery(id+"F1.imprint","IMPRINT",EDGE,{"derivedFrom":sQuery(id+"F1.wireOp",EDGE,"E227.0")}),-1.0]])]});
            var Q35;
            Q35=makeQuery(id+"F1.imprint","IMPRINT",FACE,{"disambiguationData":[TD([[makeQuery(id+"F1.imprint","IMPRINT",EDGE,{"derivedFrom":sQuery(id+"F1.wireOp",EDGE,"E190.0")}),1.0]])]});
            var Q36;
            Q36=makeQuery(id+"F1.imprint","IMPRINT",FACE,{"disambiguationData":[TD([[makeQuery(id+"F1.imprint","IMPRINT",EDGE,{"derivedFrom":sQuery(id+"F1.wireOp",EDGE,"E271.0")}),1.0]])]});
            var Q37;
            Q37=makeQuery(id+"F1.imprint","IMPRINT",FACE,{"disambiguationData":[TD([[makeQuery(id+"F1.imprint","IMPRINT",EDGE,{"derivedFrom":sQuery(id+"F1.wireOp",EDGE,"E286.0")}),1.0]])]});
            var Q38;
            Q38=makeQuery(id+"F1.imprint","IMPRINT",FACE,{"disambiguationData":[TD([[makeQuery(id+"F1.imprint","IMPRINT",EDGE,{"derivedFrom":sQuery(id+"F1.wireOp",EDGE,"E205.0")}),-1.0]])]});
            var Q39;
            Q39=makeQuery(id+"F1.imprint","IMPRINT",FACE,{"disambiguationData":[TD([[makeQuery(id+"F1.imprint","IMPRINT",EDGE,{"derivedFrom":sQuery(id+"F1.wireOp",EDGE,"E276.0")}),-1.0]])]});
            var Q40;
            Q40=makeQuery(id+"F1.imprint","IMPRINT",FACE,{"disambiguationData":[TD([[makeQuery(id+"F1.imprint","IMPRINT",EDGE,{"derivedFrom":sQuery(id+"F1.wireOp",EDGE,"E287.0")}),1.0]])]});
            var Q41;
            Q41=makeQuery(id+"F1.imprint","IMPRINT",FACE,{"disambiguationData":[TD([[makeQuery(id+"F1.imprint","IMPRINT",EDGE,{"derivedFrom":sQuery(id+"F1.wireOp",EDGE,"E269.0")}),-1.0]])]});
            var Q42;
            Q42=makeQuery(id+"F1.imprint","IMPRINT",FACE,{"disambiguationData":[TD([[makeQuery(id+"F1.imprint","IMPRINT",EDGE,{"derivedFrom":sQuery(id+"F1.wireOp",EDGE,"E221.0")}),-1.0]])]});
            var Q43;
            Q43=makeQuery(id+"F1.imprint","IMPRINT",FACE,{"disambiguationData":[TD([[makeQuery(id+"F1.imprint","IMPRINT",EDGE,{"derivedFrom":sQuery(id+"F1.wireOp",EDGE,"E288.0")}),1.0]])]});
            var Q44;
            Q44=makeQuery(id+"F1.imprint","IMPRINT",FACE,{"disambiguationData":[TD([[makeQuery(id+"F1.imprint","IMPRINT",EDGE,{"derivedFrom":sQuery(id+"F1.wireOp",EDGE,"E195.0")}),1.0]])]});
            var Q45;
            Q45=makeQuery(id+"F1.imprint","IMPRINT",FACE,{"disambiguationData":[TD([[makeQuery(id+"F1.imprint","IMPRINT",EDGE,{"derivedFrom":sQuery(id+"F1.wireOp",EDGE,"E229.0")}),-1.0]])]});
            var Q46;
            Q46=makeQuery(id+"F1.imprint","IMPRINT",FACE,{"disambiguationData":[TD([[makeQuery(id+"F1.imprint","IMPRINT",EDGE,{"derivedFrom":sQuery(id+"F1.wireOp",EDGE,"E116.0")}),-1.0]])]});
            var Q47;
            Q47=makeQuery(id+"F1.imprint","IMPRINT",FACE,{"disambiguationData":[TD([[makeQuery(id+"F1.imprint","IMPRINT",EDGE,{"derivedFrom":sQuery(id+"F1.wireOp",EDGE,"E127.0")}),1.0]])]});
            var Q48;
            Q48=makeQuery(id+"F1.imprint","IMPRINT",FACE,{"disambiguationData":[TD([[makeQuery(id+"F1.imprint","IMPRINT",EDGE,{"derivedFrom":sQuery(id+"F1.wireOp",EDGE,"E237.0")}),-1.0]])]});
            var Q49;
            Q49=makeQuery(id+"F1.imprint","IMPRINT",FACE,{"disambiguationData":[TD([[makeQuery(id+"F1.imprint","IMPRINT",EDGE,{"derivedFrom":sQuery(id+"F1.wireOp",EDGE,"E247.0")}),1.0]])]});
            var Q50;
            Q50=makeQuery(id+"F1.imprint","IMPRINT",FACE,{"disambiguationData":[TD([[makeQuery(id+"F1.imprint","IMPRINT",EDGE,{"derivedFrom":sQuery(id+"F1.wireOp",EDGE,"E241.0")}),-1.0]])]});
            var Q51;
            Q51=makeQuery(id+"F1.imprint","IMPRINT",FACE,{"disambiguationData":[TD([[makeQuery(id+"F1.imprint","IMPRINT",EDGE,{"derivedFrom":sQuery(id+"F1.wireOp",EDGE,"E185.0")}),1.0]])]});
            var Q52;
            Q52=makeQuery(id+"F1.imprint","IMPRINT",FACE,{"disambiguationData":[TD([[makeQuery(id+"F1.imprint","IMPRINT",EDGE,{"derivedFrom":sQuery(id+"F1.wireOp",EDGE,"E211.0")}),1.0]])]});
            var Q53;
            Q53=makeQuery(id+"F1.imprint","IMPRINT",FACE,{"disambiguationData":[TD([[makeQuery(id+"F1.imprint","IMPRINT",EDGE,{"derivedFrom":sQuery(id+"F1.wireOp",EDGE,"E128.0")}),1.0]])]});
            var Q54;
            Q54=makeQuery(id+"F1.imprint","IMPRINT",FACE,{"disambiguationData":[TD([[makeQuery(id+"F1.imprint","IMPRINT",EDGE,{"derivedFrom":sQuery(id+"F1.wireOp",EDGE,"E93.0")}),-1.0]])]});
            var Q55;
            Q55=makeQuery(id+"F1.imprint","IMPRINT",FACE,{"disambiguationData":[TD([[makeQuery(id+"F1.imprint","IMPRINT",EDGE,{"derivedFrom":sQuery(id+"F1.wireOp",EDGE,"E285.0")}),1.0]])]});
            var Q56;
            Q56=makeQuery(id+"F1.imprint","IMPRINT",FACE,{"disambiguationData":[TD([[makeQuery(id+"F1.imprint","IMPRINT",EDGE,{"derivedFrom":sQuery(id+"F1.wireOp",EDGE,"E94.0")}),-1.0]])]});
            var Q57;
            Q57=makeQuery(id+"F1.imprint","IMPRINT",FACE,{"disambiguationData":[TD([[makeQuery(id+"F1.imprint","IMPRINT",EDGE,{"derivedFrom":sQuery(id+"F1.wireOp",EDGE,"E169.0")}),1.0]])]});
            var Q58;
            Q58=makeQuery(id+"F1.imprint","IMPRINT",FACE,{"disambiguationData":[TD([[makeQuery(id+"F1.imprint","IMPRINT",EDGE,{"derivedFrom":sQuery(id+"F1.wireOp",EDGE,"E112.0")}),-1.0]])]});
            var Q59;
            Q59=makeQuery(id+"F1.imprint","IMPRINT",FACE,{"disambiguationData":[TD([[makeQuery(id+"F1.imprint","IMPRINT",EDGE,{"derivedFrom":sQuery(id+"F1.wireOp",EDGE,"E146.0")}),1.0]])]});
            var Q60;
            Q60=makeQuery(id+"F1.imprint","IMPRINT",FACE,{"disambiguationData":[TD([[makeQuery(id+"F1.imprint","IMPRINT",EDGE,{"derivedFrom":sQuery(id+"F1.wireOp",EDGE,"E251.0")}),-1.0]])]});
            var Q61;
            Q61=makeQuery(id+"F1.imprint","IMPRINT",FACE,{"disambiguationData":[TD([[makeQuery(id+"F1.imprint","IMPRINT",EDGE,{"derivedFrom":sQuery(id+"F1.wireOp",EDGE,"E155.0")}),-1.0]])]});
            var Q62;
            Q62=makeQuery(id+"F1.imprint","IMPRINT",FACE,{"disambiguationData":[TD([[makeQuery(id+"F1.imprint","IMPRINT",EDGE,{"derivedFrom":sQuery(id+"F1.wireOp",EDGE,"E243.0")}),-1.0]])]});
            var Q63;
            Q63=makeQuery(id+"F1.imprint","IMPRINT",FACE,{"disambiguationData":[TD([[makeQuery(id+"F1.imprint","IMPRINT",EDGE,{"derivedFrom":sQuery(id+"F1.wireOp",EDGE,"E130.0")}),1.0]])]});
            var Q64;
            Q64=makeQuery(id+"F1.imprint","IMPRINT",FACE,{"disambiguationData":[TD([[makeQuery(id+"F1.imprint","IMPRINT",EDGE,{"derivedFrom":sQuery(id+"F1.wireOp",EDGE,"E74.0")}),1.0]])]});
            var Q65;
            Q65=makeQuery(id+"F1.imprint","IMPRINT",FACE,{"disambiguationData":[TD([[makeQuery(id+"F1.imprint","IMPRINT",EDGE,{"derivedFrom":sQuery(id+"F1.wireOp",EDGE,"E284.0")}),1.0]])]});
            var Q66;
            Q66=makeQuery(id+"F1.imprint","IMPRINT",FACE,{"disambiguationData":[TD([[makeQuery(id+"F1.imprint","IMPRINT",EDGE,{"derivedFrom":sQuery(id+"F1.wireOp",EDGE,"E141.0")}),-1.0]])]});
            var Q67;
            Q67=makeQuery(id+"F1.imprint","IMPRINT",FACE,{"disambiguationData":[TD([[makeQuery(id+"F1.imprint","IMPRINT",EDGE,{"derivedFrom":sQuery(id+"F1.wireOp",EDGE,"E219.0")}),1.0]])]});
            var Q68;
            Q68=makeQuery(id+"F1.imprint","IMPRINT",FACE,{"disambiguationData":[TD([[makeQuery(id+"F1.imprint","IMPRINT",EDGE,{"derivedFrom":sQuery(id+"F1.wireOp",EDGE,"E252.0")}),1.0]])]});
            var Q69;
            Q69=makeQuery(id+"F1.imprint","IMPRINT",FACE,{"disambiguationData":[TD([[makeQuery(id+"F1.imprint","IMPRINT",EDGE,{"derivedFrom":sQuery(id+"F1.wireOp",EDGE,"E157.0")}),-1.0]])]});
            var Q70;
            Q70=makeQuery(id+"F1.imprint","IMPRINT",FACE,{"disambiguationData":[TD([[makeQuery(id+"F1.imprint","IMPRINT",EDGE,{"derivedFrom":sQuery(id+"F1.wireOp",EDGE,"E142.0")}),-1.0]])]});
            var Q71;
            Q71=makeQuery(id+"F1.imprint","IMPRINT",FACE,{"disambiguationData":[TD([[makeQuery(id+"F1.imprint","IMPRINT",EDGE,{"derivedFrom":sQuery(id+"F1.wireOp",EDGE,"E246.0")}),-1.0]])]});
            var Q72;
            Q72=makeQuery(id+"F1.imprint","IMPRINT",FACE,{"disambiguationData":[TD([[makeQuery(id+"F1.imprint","IMPRINT",EDGE,{"derivedFrom":sQuery(id+"F1.wireOp",EDGE,"E280.0")}),1.0]])]});
            var Q73;
            Q73=makeQuery(id+"F1.imprint","IMPRINT",FACE,{"disambiguationData":[TD([[makeQuery(id+"F1.imprint","IMPRINT",EDGE,{"derivedFrom":sQuery(id+"F1.wireOp",EDGE,"E267.0")}),-1.0]])]});
            var Q74;
            Q74=makeQuery(id+"F1.imprint","IMPRINT",FACE,{"disambiguationData":[TD([[makeQuery(id+"F1.imprint","IMPRINT",EDGE,{"derivedFrom":sQuery(id+"F1.wireOp",EDGE,"E75.0")}),-1.0]])]});
            var Q75;
            Q75=makeQuery(id+"F1.imprint","IMPRINT",FACE,{"disambiguationData":[TD([[makeQuery(id+"F1.imprint","IMPRINT",EDGE,{"derivedFrom":sQuery(id+"F1.wireOp",EDGE,"E234.0")}),1.0]])]});
            var Q76;
            Q76=makeQuery(id+"F1.imprint","IMPRINT",FACE,{"disambiguationData":[TD([[makeQuery(id+"F1.imprint","IMPRINT",EDGE,{"derivedFrom":sQuery(id+"F1.wireOp",EDGE,"E166.0")}),1.0]])]});
            var Q77;
            Q77=makeQuery(id+"F1.imprint","IMPRINT",FACE,{"disambiguationData":[TD([[makeQuery(id+"F1.imprint","IMPRINT",EDGE,{"derivedFrom":sQuery(id+"F1.wireOp",EDGE,"E233.0")}),1.0]])]});
            var Q78;
            Q78=makeQuery(id+"F1.imprint","IMPRINT",FACE,{"disambiguationData":[TD([[makeQuery(id+"F1.imprint","IMPRINT",EDGE,{"derivedFrom":sQuery(id+"F1.wireOp",EDGE,"E111.0")}),-1.0]])]});
            var Q79;
            Q79=makeQuery(id+"F1.imprint","IMPRINT",FACE,{"disambiguationData":[TD([[makeQuery(id+"F1.imprint","IMPRINT",EDGE,{"derivedFrom":sQuery(id+"F1.wireOp",EDGE,"E72.0")}),-1.0]])]});
            var Q80;
            Q80=makeQuery(id+"F1.imprint","IMPRINT",FACE,{"disambiguationData":[TD([[makeQuery(id+"F1.imprint","IMPRINT",EDGE,{"derivedFrom":sQuery(id+"F1.wireOp",EDGE,"E159.0")}),-1.0]])]});
            var Q81;
            Q81=makeQuery(id+"F1.imprint","IMPRINT",FACE,{"disambiguationData":[TD([[makeQuery(id+"F1.imprint","IMPRINT",EDGE,{"derivedFrom":sQuery(id+"F1.wireOp",EDGE,"E248.0")}),1.0]])]});
            var Q82;
            Q82=makeQuery(id+"F1.imprint","IMPRINT",FACE,{"disambiguationData":[TD([[makeQuery(id+"F1.imprint","IMPRINT",EDGE,{"derivedFrom":sQuery(id+"F1.wireOp",EDGE,"E99.0")}),1.0]])]});
            var Q83;
            Q83=makeQuery(id+"F1.imprint","IMPRINT",FACE,{"disambiguationData":[TD([[makeQuery(id+"F1.imprint","IMPRINT",EDGE,{"derivedFrom":sQuery(id+"F1.wireOp",EDGE,"E71.0")}),1.0]])]});
            var Q84;
            Q84=makeQuery(id+"F1.imprint","IMPRINT",FACE,{"disambiguationData":[TD([[makeQuery(id+"F1.imprint","IMPRINT",EDGE,{"derivedFrom":sQuery(id+"F1.wireOp",EDGE,"E118.0")}),-1.0]])]});
            var Q85;
            Q85=makeQuery(id+"F1.imprint","IMPRINT",FACE,{"disambiguationData":[TD([[makeQuery(id+"F1.imprint","IMPRINT",EDGE,{"derivedFrom":sQuery(id+"F1.wireOp",EDGE,"E225.0")}),-1.0]])]});
            var Q86;
            Q86=makeQuery(id+"F1.imprint","IMPRINT",FACE,{"disambiguationData":[TD([[makeQuery(id+"F1.imprint","IMPRINT",EDGE,{"derivedFrom":sQuery(id+"F1.wireOp",EDGE,"E129.0")}),1.0]])]});
            var Q87;
            Q87=makeQuery(id+"F1.imprint","IMPRINT",FACE,{"disambiguationData":[TD([[makeQuery(id+"F1.imprint","IMPRINT",EDGE,{"derivedFrom":sQuery(id+"F1.wireOp",EDGE,"E275.0")}),1.0]])]});
            var Q88;
            Q88=makeQuery(id+"F1.imprint","IMPRINT",FACE,{"disambiguationData":[TD([[makeQuery(id+"F1.imprint","IMPRINT",EDGE,{"derivedFrom":sQuery(id+"F1.wireOp",EDGE,"E279.0")}),1.0]])]});
            var Q89;
            {var subQ4=sQuery(id+"F1.wireOp",EDGE,"E114.1");Q89=makeQuery(id+"F1.imprint","IMPRINT",FACE,{"disambiguationData":[TD([[makeQuery(id+"F1.imprint","IMPRINT",EDGE,{"derivedFrom":subQ4}),1.0]])]});}
            var Q90;
            {var subQ3=sQuery(id+"F1.wireOp",EDGE,"E327");Q90=makeQuery(id+"F1.imprint","IMPRINT",FACE,{"disambiguationData":[TD([[makeQuery(id+"F1.imprint","IMPRINT",EDGE,{"derivedFrom":subQ3}),1.0]])]});}
            var Q91;
            {var subQ5=sQuery(id+"F1.wireOp",EDGE,"E325");Q91=makeQuery(id+"F1.imprint","IMPRINT",FACE,{"disambiguationData":[TD([[makeQuery(id+"F1.imprint","IMPRINT",EDGE,{"derivedFrom":subQ5}),-1.0]])]});}
            var Q92;
            {var subQ0=sQuery(id+"F1.wireOp",EDGE,"E313");Q92=makeQuery(id+"F1.imprint","IMPRINT",FACE,{"disambiguationData":[TD([[makeQuery(id+"F1.imprint","IMPRINT",EDGE,{"derivedFrom":subQ0}),-1.0]])]});}
            var Q93;
            {var subQ0=sQuery(id+"F1.wireOp",EDGE,"E314");Q93=makeQuery(id+"F1.imprint","IMPRINT",FACE,{"disambiguationData":[TD([[makeQuery(id+"F1.imprint","IMPRINT",EDGE,{"derivedFrom":subQ0}),1.0]])]});}
            var Q94;
            {var subQ0=sQuery(id+"F1.wireOp",EDGE,"E100.2");Q94=makeQuery(id+"F1.imprint","IMPRINT",FACE,{"disambiguationData":[TD([[makeQuery(id+"F1.imprint","IMPRINT",EDGE,{"derivedFrom":subQ0}),-1.0]])]});}
            var Q95;
            {var subQ15=sQuery(id+"F1.wireOp",EDGE,"E291");Q95=makeQuery(id+"F1.imprint","IMPRINT",FACE,{"disambiguationData":[TD([[makeQuery(id+"F1.imprint","IMPRINT",EDGE,{"derivedFrom":subQ15}),-1.0]])]});}
            var Q96;
            {var subQ4=sQuery(id+"F1.wireOp",EDGE,"E182.1");Q96=makeQuery(id+"F1.imprint","IMPRINT",FACE,{"disambiguationData":[TD([[makeQuery(id+"F1.imprint","IMPRINT",EDGE,{"derivedFrom":subQ4}),-1.0]])]});}
            extrude(context, id + "F3", {"entities" : qUnion([Q0, Q1, Q2, Q3, Q4, Q5, Q6, Q7, Q8, Q9, Q10, Q11, Q12, Q13, Q14, Q15, Q16, Q17, Q18, Q19, Q20, Q21, Q22, Q23, Q24, Q25, Q26, Q27, Q28, Q29, Q30, Q31, Q32, Q33, Q34, Q35, Q36, Q37, Q38, Q39, Q40, Q41, Q42, Q43, Q44, Q45, Q46, Q47, Q48, Q49, Q50, Q51, Q52, Q53, Q54, Q55, Q56, Q57, Q58, Q59, Q60, Q61, Q62, Q63, Q64, Q65, Q66, Q67, Q68, Q69, Q70, Q71, Q72, Q73, Q74, Q75, Q76, Q77, Q78, Q79, Q80, Q81, Q82, Q83, Q84, Q85, Q86, Q87, Q88, Q89, Q90, Q91, Q92, Q93, Q94, Q95, Q96]), "operationType" : NewBodyOperationType.REMOVE, "depth" : 66.04 * mm, "offsetDistance" : 25.4 * mm});
        }
        {
            var Q0;
            Q0=makeQuery(id+"F2.opExtrude","SWEPT_BODY",BODY,{"disambiguationData":[OSD([sQuery(id+"F0.wireOp",EDGE,"E3"),sQuery(id+"F0.wireOp",EDGE,"E5"),sQuery(id+"F0.wireOp",EDGE,"E8"),sQuery(id+"F0.wireOp",EDGE,"E10")])]});
            var Q1;
            Q1=makeQuery(id+"F3.boolean.opBoolean","INTERSECT",VERTEX,{"derivedFrom":[makeQuery(id+"F2.opExtrude","SWEPT_FACE",FACE,{"disambiguationData":[OSD([sQuery(id+"F0.wireOp",EDGE,"E10")])]}),makeQuery(id+"F3.opExtrude","SWEPT_FACE",FACE,{"disambiguationData":[OSD([sQuery(id+"F1.wireOp",EDGE,"E185.0")])]}),makeQuery(id+"F3.opExtrude","SWEPT_FACE",FACE,{"disambiguationData":[OSD([sQuery(id+"F1.wireOp",EDGE,"E185.1")])]})]});
            transform(context, id + "F4", {"entities" : qUnion([Q0]), "transformType" : TransformType.SCALE_UNIFORMLY, "scale" : 0.6, "scalePoint" : qUnion([Q1]), "makeCopy" : false});
        }
    });
